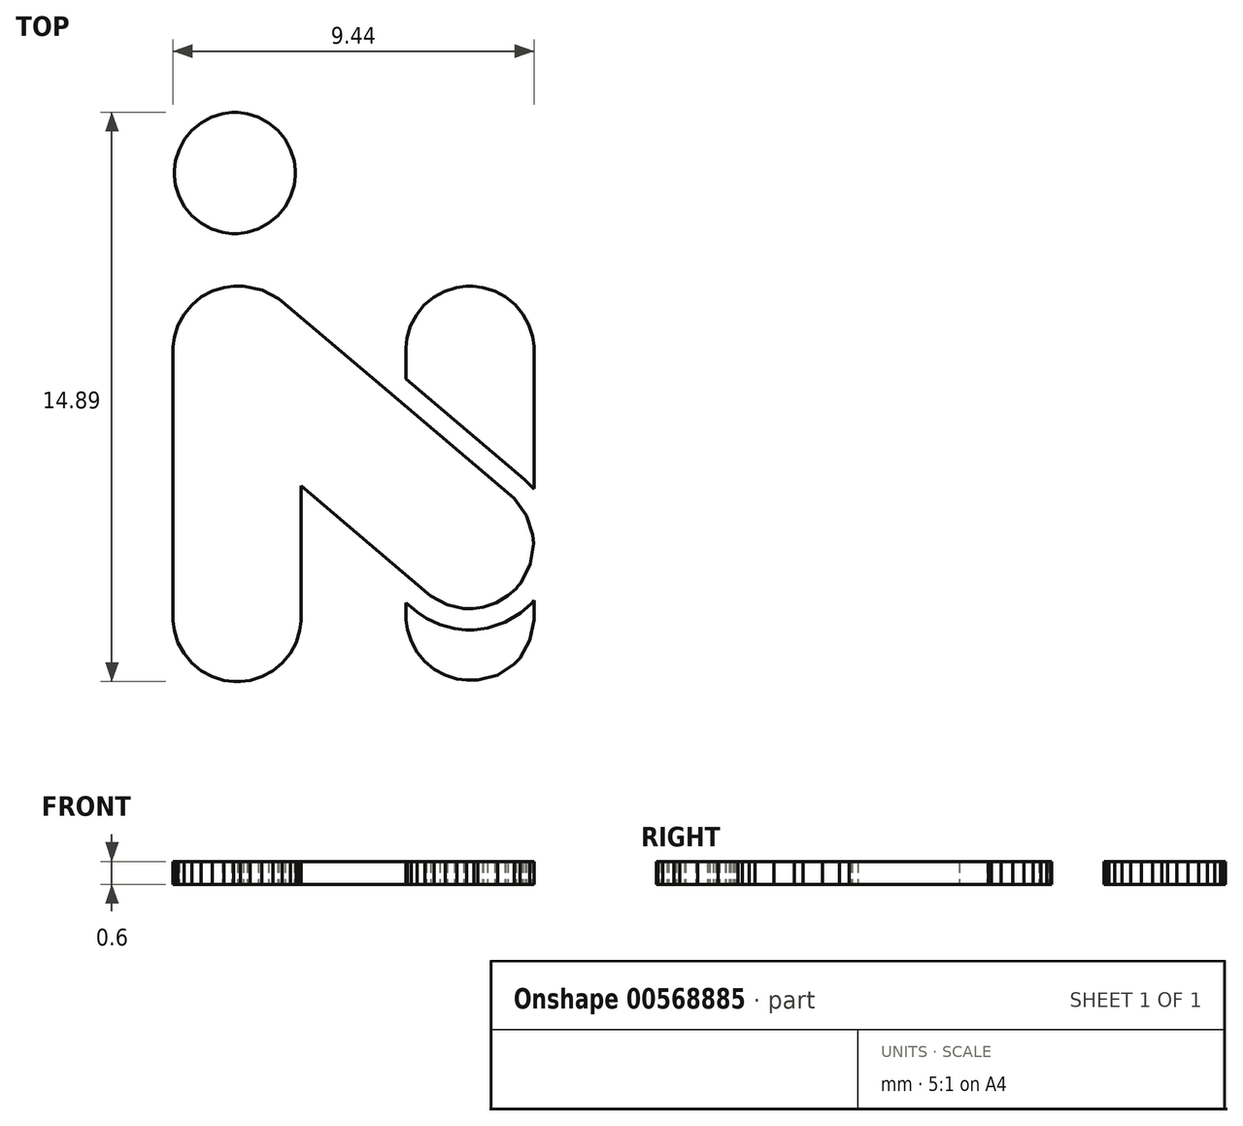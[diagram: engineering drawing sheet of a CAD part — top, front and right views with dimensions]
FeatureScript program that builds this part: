
annotation { "Feature Type Name" : "Feature", "Feature Type Description" : "" }
export const myFeature = defineFeature(function(context is Context, id is Id, definition is map)
    precondition{}
    {
        {
            var Q0;
            Q0=qCreatedBy(makeId("Top.planeOp"),FACE);
            var sketch = newSketch(context, id + "F0", { "sketchPlane" : qUnion([Q0])});
            skLineSegment(sketch, "E0", {"start": v(1.16, -1.13) * mm, "end": v(1.14, -1.15) * mm});
            skLineSegment(sketch, "E1", {"start": v(1.14, -1.15) * mm, "end": v(1.03, -1.22) * mm});
            skLineSegment(sketch, "E2", {"start": v(1.03, -1.22) * mm, "end": v(0.9, -1.25) * mm});
            skLineSegment(sketch, "E3", {"start": v(0.9, -1.25) * mm, "end": v(0.88, -1.26) * mm});
            skLineSegment(sketch, "E4", {"start": v(0.88, -1.26) * mm, "end": v(0.88, -1.26) * mm});
            skLineSegment(sketch, "E5", {"start": v(0.88, -1.26) * mm, "end": v(0.87, -1.26) * mm});
            skLineSegment(sketch, "E6", {"start": v(0.87, -1.26) * mm, "end": v(0.86, -1.26) * mm});
            skLineSegment(sketch, "E7", {"start": v(0.86, -1.26) * mm, "end": v(0.85, -1.26) * mm});
            skLineSegment(sketch, "E8", {"start": v(0.85, -1.26) * mm, "end": v(0.83, -1.26) * mm});
            skLineSegment(sketch, "E9", {"start": v(0.83, -1.26) * mm, "end": v(0.77, -1.25) * mm});
            skLineSegment(sketch, "E10", {"start": v(0.77, -1.25) * mm, "end": v(0.7, -1.22) * mm});
            skLineSegment(sketch, "E11", {"start": v(0.7, -1.22) * mm, "end": v(0.62, -1.18) * mm});
            skLineSegment(sketch, "E12", {"start": v(0.62, -1.18) * mm, "end": v(0.56, -1.13) * mm});
            skLineSegment(sketch, "E13", {"start": v(0.56, -1.13) * mm, "end": v(0.5, -1.07) * mm});
            skLineSegment(sketch, "E14", {"start": v(0.5, -1.07) * mm, "end": v(0.47, -1) * mm});
            skLineSegment(sketch, "E15", {"start": v(0.47, -1) * mm, "end": v(0.44, -0.92) * mm});
            skLineSegment(sketch, "E16", {"start": v(0.44, -0.92) * mm, "end": v(0.43, -0.86) * mm});
            skLineSegment(sketch, "E17", {"start": v(0.43, -0.86) * mm, "end": v(0.43, -0.84) * mm});
            skLineSegment(sketch, "E18", {"start": v(0.43, -0.84) * mm, "end": v(0.43, -0.75) * mm});
            skLineSegment(sketch, "E19", {"start": v(0.43, -0.75) * mm, "end": v(0.49, -0.8) * mm});
            skLineSegment(sketch, "E20", {"start": v(0.49, -0.8) * mm, "end": v(0.5, -0.8) * mm});
            skLineSegment(sketch, "E21", {"start": v(0.5, -0.8) * mm, "end": v(0.57, -0.85) * mm});
            skLineSegment(sketch, "E22", {"start": v(0.57, -0.85) * mm, "end": v(0.66, -0.9) * mm});
            skLineSegment(sketch, "E23", {"start": v(0.66, -0.9) * mm, "end": v(0.75, -0.92) * mm});
            skLineSegment(sketch, "E24", {"start": v(0.75, -0.92) * mm, "end": v(0.83, -0.93) * mm});
            skLineSegment(sketch, "E25", {"start": v(0.83, -0.93) * mm, "end": v(0.85, -0.93) * mm});
            skLineSegment(sketch, "E26", {"start": v(0.85, -0.93) * mm, "end": v(0.88, -0.93) * mm});
            skLineSegment(sketch, "E27", {"start": v(0.88, -0.93) * mm, "end": v(0.97, -0.91) * mm});
            skLineSegment(sketch, "E28", {"start": v(0.97, -0.91) * mm, "end": v(1.08, -0.88) * mm});
            skLineSegment(sketch, "E29", {"start": v(1.08, -0.88) * mm, "end": v(1.19, -0.81) * mm});
            skLineSegment(sketch, "E30", {"start": v(1.19, -0.81) * mm, "end": v(1.25, -0.75) * mm});
            skLineSegment(sketch, "E31", {"start": v(1.25, -0.75) * mm, "end": v(1.27, -0.73) * mm});
            skLineSegment(sketch, "E32", {"start": v(1.27, -0.73) * mm, "end": v(1.27, -0.83) * mm});
            skLineSegment(sketch, "E33", {"start": v(1.27, -0.83) * mm, "end": v(1.27, -0.86) * mm});
            skLineSegment(sketch, "E34", {"start": v(1.27, -0.86) * mm, "end": v(1.25, -1) * mm});
            skLineSegment(sketch, "E35", {"start": v(1.25, -1) * mm, "end": v(1.18, -1.11) * mm});
            skLineSegment(sketch, "E36", {"start": v(1.18, -1.11) * mm, "end": v(1.16, -1.13) * mm});
            skLineSegment(sketch, "E37", {"start": v(-0.25, 0.02) * mm, "end": v(-0.25, -0.85) * mm});
            skLineSegment(sketch, "E38", {"start": v(-0.25, -0.85) * mm, "end": v(-0.25, -0.87) * mm});
            skLineSegment(sketch, "E39", {"start": v(-0.25, -0.87) * mm, "end": v(-0.26, -0.93) * mm});
            skLineSegment(sketch, "E40", {"start": v(-0.26, -0.93) * mm, "end": v(-0.28, -1) * mm});
            skLineSegment(sketch, "E41", {"start": v(-0.28, -1) * mm, "end": v(-0.32, -1.08) * mm});
            skLineSegment(sketch, "E42", {"start": v(-0.32, -1.08) * mm, "end": v(-0.37, -1.14) * mm});
            skLineSegment(sketch, "E43", {"start": v(-0.37, -1.14) * mm, "end": v(-0.44, -1.2) * mm});
            skLineSegment(sketch, "E44", {"start": v(-0.44, -1.2) * mm, "end": v(-0.5, -1.23) * mm});
            skLineSegment(sketch, "E45", {"start": v(-0.5, -1.23) * mm, "end": v(-0.59, -1.26) * mm});
            skLineSegment(sketch, "E46", {"start": v(-0.59, -1.26) * mm, "end": v(-0.65, -1.26) * mm});
            skLineSegment(sketch, "E47", {"start": v(-0.65, -1.26) * mm, "end": v(-0.67, -1.26) * mm});
            skLineSegment(sketch, "E48", {"start": v(-0.67, -1.26) * mm, "end": v(-0.7, -1.26) * mm});
            skLineSegment(sketch, "E49", {"start": v(-0.7, -1.26) * mm, "end": v(-0.75, -1.26) * mm});
            skLineSegment(sketch, "E50", {"start": v(-0.75, -1.26) * mm, "end": v(-0.83, -1.23) * mm});
            skLineSegment(sketch, "E51", {"start": v(-0.83, -1.23) * mm, "end": v(-0.9, -1.2) * mm});
            skLineSegment(sketch, "E52", {"start": v(-0.9, -1.2) * mm, "end": v(-0.97, -1.14) * mm});
            skLineSegment(sketch, "E53", {"start": v(-0.97, -1.14) * mm, "end": v(-1.02, -1.08) * mm});
            skLineSegment(sketch, "E54", {"start": v(-1.02, -1.08) * mm, "end": v(-1.06, -1) * mm});
            skLineSegment(sketch, "E55", {"start": v(-1.06, -1) * mm, "end": v(-1.08, -0.93) * mm});
            skLineSegment(sketch, "E56", {"start": v(-1.08, -0.93) * mm, "end": v(-1.09, -0.87) * mm});
            skLineSegment(sketch, "E57", {"start": v(-1.09, -0.87) * mm, "end": v(-1.09, -0.85) * mm});
            skLineSegment(sketch, "E58", {"start": v(-1.09, -0.85) * mm, "end": v(-1.09, 0.9) * mm});
            skLineSegment(sketch, "E59", {"start": v(-1.09, 0.9) * mm, "end": v(-1.09, 0.92) * mm});
            skLineSegment(sketch, "E60", {"start": v(-1.09, 0.92) * mm, "end": v(-1.08, 0.99) * mm});
            skLineSegment(sketch, "E61", {"start": v(-1.08, 0.99) * mm, "end": v(-1.06, 1.07) * mm});
            skLineSegment(sketch, "E62", {"start": v(-1.06, 1.07) * mm, "end": v(-1.02, 1.14) * mm});
            skLineSegment(sketch, "E63", {"start": v(-1.02, 1.14) * mm, "end": v(-0.97, 1.2) * mm});
            skLineSegment(sketch, "E64", {"start": v(-0.97, 1.2) * mm, "end": v(-0.9, 1.25) * mm});
            skLineSegment(sketch, "E65", {"start": v(-0.9, 1.25) * mm, "end": v(-0.83, 1.29) * mm});
            skLineSegment(sketch, "E66", {"start": v(-0.83, 1.29) * mm, "end": v(-0.75, 1.31) * mm});
            skLineSegment(sketch, "E67", {"start": v(-0.75, 1.31) * mm, "end": v(-0.7, 1.32) * mm});
            skLineSegment(sketch, "E68", {"start": v(-0.7, 1.32) * mm, "end": v(-0.67, 1.32) * mm});
            skLineSegment(sketch, "E69", {"start": v(-0.67, 1.32) * mm, "end": v(-0.67, 1.32) * mm});
            skLineSegment(sketch, "E70", {"start": v(-0.67, 1.32) * mm, "end": v(-0.66, 1.32) * mm});
            skLineSegment(sketch, "E71", {"start": v(-0.66, 1.32) * mm, "end": v(-0.66, 1.32) * mm});
            skLineSegment(sketch, "E72", {"start": v(-0.66, 1.32) * mm, "end": v(-0.65, 1.32) * mm});
            skLineSegment(sketch, "E73", {"start": v(-0.65, 1.32) * mm, "end": v(-0.65, 1.32) * mm});
            skLineSegment(sketch, "E74", {"start": v(-0.65, 1.32) * mm, "end": v(-0.63, 1.32) * mm});
            skLineSegment(sketch, "E75", {"start": v(-0.63, 1.32) * mm, "end": v(-0.5, 1.3) * mm});
            skLineSegment(sketch, "E76", {"start": v(-0.5, 1.3) * mm, "end": v(-0.4, 1.24) * mm});
            skLineSegment(sketch, "E77", {"start": v(-0.4, 1.24) * mm, "end": v(-0.38, 1.22) * mm});
            skLineSegment(sketch, "E78", {"start": v(-0.38, 1.22) * mm, "end": v(0.32, 0.63) * mm});
            skLineSegment(sketch, "E79", {"start": v(0.32, 0.63) * mm, "end": v(0.36, 0.68) * mm});
            skLineSegment(sketch, "E80", {"start": v(0.36, 0.68) * mm, "end": v(0.32, 0.63) * mm});
            skLineSegment(sketch, "E81", {"start": v(0.32, 0.63) * mm, "end": v(1.12, -0.05) * mm});
            skLineSegment(sketch, "E82", {"start": v(1.12, -0.05) * mm, "end": v(1.14, -0.07) * mm});
            skLineSegment(sketch, "E83", {"start": v(1.14, -0.07) * mm, "end": v(1.22, -0.18) * mm});
            skLineSegment(sketch, "E84", {"start": v(1.22, -0.18) * mm, "end": v(1.27, -0.3) * mm});
            skLineSegment(sketch, "E85", {"start": v(1.27, -0.3) * mm, "end": v(1.27, -0.33) * mm});
            skLineSegment(sketch, "E86", {"start": v(1.27, -0.33) * mm, "end": v(1.27, -0.36) * mm});
            skLineSegment(sketch, "E87", {"start": v(1.27, -0.36) * mm, "end": v(1.25, -0.5) * mm});
            skLineSegment(sketch, "E88", {"start": v(1.25, -0.5) * mm, "end": v(1.19, -0.62) * mm});
            skLineSegment(sketch, "E89", {"start": v(1.19, -0.62) * mm, "end": v(1.17, -0.64) * mm});
            skLineSegment(sketch, "E90", {"start": v(1.17, -0.64) * mm, "end": v(1.15, -0.66) * mm});
            skLineSegment(sketch, "E91", {"start": v(1.15, -0.66) * mm, "end": v(1.1, -0.7) * mm});
            skLineSegment(sketch, "E92", {"start": v(1.1, -0.7) * mm, "end": v(1.03, -0.75) * mm});
            skLineSegment(sketch, "E93", {"start": v(1.03, -0.75) * mm, "end": v(0.94, -0.78) * mm});
            skLineSegment(sketch, "E94", {"start": v(0.94, -0.78) * mm, "end": v(0.87, -0.79) * mm});
            skLineSegment(sketch, "E95", {"start": v(0.87, -0.79) * mm, "end": v(0.85, -0.79) * mm});
            skLineSegment(sketch, "E96", {"start": v(0.85, -0.79) * mm, "end": v(0.81, -0.79) * mm});
            skLineSegment(sketch, "E97", {"start": v(0.81, -0.79) * mm, "end": v(0.7, -0.76) * mm});
            skLineSegment(sketch, "E98", {"start": v(0.7, -0.76) * mm, "end": v(0.6, -0.7) * mm});
            skLineSegment(sketch, "E99", {"start": v(0.6, -0.7) * mm, "end": v(0.58, -0.69) * mm});
            skLineSegment(sketch, "E100", {"start": v(0.58, -0.69) * mm, "end": v(0.41, -0.54) * mm});
            skLineSegment(sketch, "E101", {"start": v(0.41, -0.54) * mm, "end": v(-0.25, 0.02) * mm});
            skLineSegment(sketch, "E102", {"start": v(0.85, 1.32) * mm, "end": v(0.85, 1.32) * mm});
            skLineSegment(sketch, "E103", {"start": v(0.85, 1.32) * mm, "end": v(0.87, 1.32) * mm});
            skLineSegment(sketch, "E104", {"start": v(0.87, 1.32) * mm, "end": v(0.94, 1.31) * mm});
            skLineSegment(sketch, "E105", {"start": v(0.94, 1.31) * mm, "end": v(1.02, 1.29) * mm});
            skLineSegment(sketch, "E106", {"start": v(1.02, 1.29) * mm, "end": v(1.09, 1.25) * mm});
            skLineSegment(sketch, "E107", {"start": v(1.09, 1.25) * mm, "end": v(1.15, 1.2) * mm});
            skLineSegment(sketch, "E108", {"start": v(1.15, 1.2) * mm, "end": v(1.2, 1.14) * mm});
            skLineSegment(sketch, "E109", {"start": v(1.2, 1.14) * mm, "end": v(1.24, 1.07) * mm});
            skLineSegment(sketch, "E110", {"start": v(1.24, 1.07) * mm, "end": v(1.26, 1) * mm});
            skLineSegment(sketch, "E111", {"start": v(1.26, 1) * mm, "end": v(1.27, 0.93) * mm});
            skLineSegment(sketch, "E112", {"start": v(1.27, 0.93) * mm, "end": v(1.27, 0.9) * mm});
            skLineSegment(sketch, "E113", {"start": v(1.27, 0.9) * mm, "end": v(1.27, 0) * mm});
            skLineSegment(sketch, "E114", {"start": v(1.27, 0) * mm, "end": v(1.27, 0) * mm});
            skLineSegment(sketch, "E115", {"start": v(1.27, 0) * mm, "end": v(1.22, 0.05) * mm});
            skLineSegment(sketch, "E116", {"start": v(1.22, 0.05) * mm, "end": v(1.21, 0.06) * mm});
            skLineSegment(sketch, "E117", {"start": v(1.21, 0.06) * mm, "end": v(0.43, 0.72) * mm});
            skLineSegment(sketch, "E118", {"start": v(0.43, 0.72) * mm, "end": v(0.43, 0.9) * mm});
            skLineSegment(sketch, "E119", {"start": v(0.43, 0.9) * mm, "end": v(0.43, 0.92) * mm});
            skLineSegment(sketch, "E120", {"start": v(0.43, 0.92) * mm, "end": v(0.44, 0.98) * mm});
            skLineSegment(sketch, "E121", {"start": v(0.44, 0.98) * mm, "end": v(0.47, 1.06) * mm});
            skLineSegment(sketch, "E122", {"start": v(0.47, 1.06) * mm, "end": v(0.5, 1.13) * mm});
            skLineSegment(sketch, "E123", {"start": v(0.5, 1.13) * mm, "end": v(0.55, 1.2) * mm});
            skLineSegment(sketch, "E124", {"start": v(0.55, 1.2) * mm, "end": v(0.62, 1.25) * mm});
            skLineSegment(sketch, "E125", {"start": v(0.62, 1.25) * mm, "end": v(0.69, 1.29) * mm});
            skLineSegment(sketch, "E126", {"start": v(0.69, 1.29) * mm, "end": v(0.77, 1.31) * mm});
            skLineSegment(sketch, "E127", {"start": v(0.77, 1.31) * mm, "end": v(0.83, 1.32) * mm});
            skLineSegment(sketch, "E128", {"start": v(0.83, 1.32) * mm, "end": v(0.85, 1.32) * mm});
            skLineSegment(sketch, "E129", {"start": v(1.41, 0.9) * mm, "end": v(1.41, 0.94) * mm});
            skLineSegment(sketch, "E130", {"start": v(1.41, 0.94) * mm, "end": v(1.4, 1.02) * mm});
            skLineSegment(sketch, "E131", {"start": v(1.4, 1.02) * mm, "end": v(1.37, 1.12) * mm});
            skLineSegment(sketch, "E132", {"start": v(1.37, 1.12) * mm, "end": v(1.31, 1.22) * mm});
            skLineSegment(sketch, "E133", {"start": v(1.31, 1.22) * mm, "end": v(1.25, 1.3) * mm});
            skLineSegment(sketch, "E134", {"start": v(1.25, 1.3) * mm, "end": v(1.16, 1.37) * mm});
            skLineSegment(sketch, "E135", {"start": v(1.16, 1.37) * mm, "end": v(1.07, 1.42) * mm});
            skLineSegment(sketch, "E136", {"start": v(1.07, 1.42) * mm, "end": v(0.96, 1.45) * mm});
            skLineSegment(sketch, "E137", {"start": v(0.96, 1.45) * mm, "end": v(0.88, 1.46) * mm});
            skLineSegment(sketch, "E138", {"start": v(0.88, 1.46) * mm, "end": v(0.85, 1.46) * mm});
            skLineSegment(sketch, "E139", {"start": v(0.85, 1.46) * mm, "end": v(0.85, 1.46) * mm});
            skLineSegment(sketch, "E140", {"start": v(0.85, 1.46) * mm, "end": v(0.82, 1.46) * mm});
            skLineSegment(sketch, "E141", {"start": v(0.82, 1.46) * mm, "end": v(0.74, 1.45) * mm});
            skLineSegment(sketch, "E142", {"start": v(0.74, 1.45) * mm, "end": v(0.63, 1.41) * mm});
            skLineSegment(sketch, "E143", {"start": v(0.63, 1.41) * mm, "end": v(0.54, 1.36) * mm});
            skLineSegment(sketch, "E144", {"start": v(0.54, 1.36) * mm, "end": v(0.46, 1.3) * mm});
            skLineSegment(sketch, "E145", {"start": v(0.46, 1.3) * mm, "end": v(0.39, 1.2) * mm});
            skLineSegment(sketch, "E146", {"start": v(0.39, 1.2) * mm, "end": v(0.34, 1.11) * mm});
            skLineSegment(sketch, "E147", {"start": v(0.34, 1.11) * mm, "end": v(0.3, 1) * mm});
            skLineSegment(sketch, "E148", {"start": v(0.3, 1) * mm, "end": v(0.3, 0.93) * mm});
            skLineSegment(sketch, "E149", {"start": v(0.3, 0.93) * mm, "end": v(0.3, 0.9) * mm});
            skLineSegment(sketch, "E150", {"start": v(0.3, 0.9) * mm, "end": v(0.3, 0.83) * mm});
            skLineSegment(sketch, "E151", {"start": v(0.3, 0.83) * mm, "end": v(-0.29, 1.33) * mm});
            skLineSegment(sketch, "E152", {"start": v(-0.29, 1.33) * mm, "end": v(-0.3, 1.34) * mm});
            skLineSegment(sketch, "E153", {"start": v(-0.3, 1.34) * mm, "end": v(-0.37, 1.38) * mm});
            skLineSegment(sketch, "E154", {"start": v(-0.37, 1.38) * mm, "end": v(-0.46, 1.43) * mm});
            skLineSegment(sketch, "E155", {"start": v(-0.46, 1.43) * mm, "end": v(-0.55, 1.45) * mm});
            skLineSegment(sketch, "E156", {"start": v(-0.55, 1.45) * mm, "end": v(-0.62, 1.46) * mm});
            skLineSegment(sketch, "E157", {"start": v(-0.62, 1.46) * mm, "end": v(-0.65, 1.46) * mm});
            skLineSegment(sketch, "E158", {"start": v(-0.65, 1.46) * mm, "end": v(-0.65, 1.46) * mm});
            skLineSegment(sketch, "E159", {"start": v(-0.65, 1.46) * mm, "end": v(-0.67, 1.46) * mm});
            skLineSegment(sketch, "E160", {"start": v(-0.67, 1.46) * mm, "end": v(-0.67, 1.46) * mm});
            skLineSegment(sketch, "E161", {"start": v(-0.67, 1.46) * mm, "end": v(-0.7, 1.46) * mm});
            skLineSegment(sketch, "E162", {"start": v(-0.7, 1.46) * mm, "end": v(-0.78, 1.45) * mm});
            skLineSegment(sketch, "E163", {"start": v(-0.78, 1.45) * mm, "end": v(-0.89, 1.42) * mm});
            skLineSegment(sketch, "E164", {"start": v(-0.89, 1.42) * mm, "end": v(-0.98, 1.36) * mm});
            skLineSegment(sketch, "E165", {"start": v(-0.98, 1.36) * mm, "end": v(-1.06, 1.3) * mm});
            skLineSegment(sketch, "E166", {"start": v(-1.06, 1.3) * mm, "end": v(-1.13, 1.21) * mm});
            skLineSegment(sketch, "E167", {"start": v(-1.13, 1.21) * mm, "end": v(-1.18, 1.12) * mm});
            skLineSegment(sketch, "E168", {"start": v(-1.18, 1.12) * mm, "end": v(-1.22, 1.01) * mm});
            skLineSegment(sketch, "E169", {"start": v(-1.22, 1.01) * mm, "end": v(-1.23, 0.93) * mm});
            skLineSegment(sketch, "E170", {"start": v(-1.23, 0.93) * mm, "end": v(-1.23, 0.9) * mm});
            skLineSegment(sketch, "E171", {"start": v(-1.23, 0.9) * mm, "end": v(-1.23, -0.85) * mm});
            skLineSegment(sketch, "E172", {"start": v(-1.23, -0.85) * mm, "end": v(-1.23, -0.87) * mm});
            skLineSegment(sketch, "E173", {"start": v(-1.23, -0.87) * mm, "end": v(-1.22, -0.96) * mm});
            skLineSegment(sketch, "E174", {"start": v(-1.22, -0.96) * mm, "end": v(-1.18, -1.06) * mm});
            skLineSegment(sketch, "E175", {"start": v(-1.18, -1.06) * mm, "end": v(-1.13, -1.16) * mm});
            skLineSegment(sketch, "E176", {"start": v(-1.13, -1.16) * mm, "end": v(-1.06, -1.24) * mm});
            skLineSegment(sketch, "E177", {"start": v(-1.06, -1.24) * mm, "end": v(-0.98, -1.3) * mm});
            skLineSegment(sketch, "E178", {"start": v(-0.98, -1.3) * mm, "end": v(-0.89, -1.36) * mm});
            skLineSegment(sketch, "E179", {"start": v(-0.89, -1.36) * mm, "end": v(-0.78, -1.4) * mm});
            skLineSegment(sketch, "E180", {"start": v(-0.78, -1.4) * mm, "end": v(-0.7, -1.4) * mm});
            skLineSegment(sketch, "E181", {"start": v(-0.7, -1.4) * mm, "end": v(-0.67, -1.4) * mm});
            skLineSegment(sketch, "E182", {"start": v(-0.67, -1.4) * mm, "end": v(-0.64, -1.4) * mm});
            skLineSegment(sketch, "E183", {"start": v(-0.64, -1.4) * mm, "end": v(-0.56, -1.4) * mm});
            skLineSegment(sketch, "E184", {"start": v(-0.56, -1.4) * mm, "end": v(-0.45, -1.36) * mm});
            skLineSegment(sketch, "E185", {"start": v(-0.45, -1.36) * mm, "end": v(-0.36, -1.3) * mm});
            skLineSegment(sketch, "E186", {"start": v(-0.36, -1.3) * mm, "end": v(-0.27, -1.24) * mm});
            skLineSegment(sketch, "E187", {"start": v(-0.27, -1.24) * mm, "end": v(-0.2, -1.16) * mm});
            skLineSegment(sketch, "E188", {"start": v(-0.2, -1.16) * mm, "end": v(-0.16, -1.06) * mm});
            skLineSegment(sketch, "E189", {"start": v(-0.16, -1.06) * mm, "end": v(-0.12, -0.96) * mm});
            skLineSegment(sketch, "E190", {"start": v(-0.12, -0.96) * mm, "end": v(-0.11, -0.87) * mm});
            skLineSegment(sketch, "E191", {"start": v(-0.11, -0.87) * mm, "end": v(-0.11, -0.85) * mm});
            skLineSegment(sketch, "E192", {"start": v(-0.11, -0.85) * mm, "end": v(-0.11, -0.28) * mm});
            skLineSegment(sketch, "E193", {"start": v(-0.11, -0.28) * mm, "end": v(0.3, -0.63) * mm});
            skLineSegment(sketch, "E194", {"start": v(0.3, -0.63) * mm, "end": v(0.3, -0.84) * mm});
            skLineSegment(sketch, "E195", {"start": v(0.3, -0.84) * mm, "end": v(0.3, -0.87) * mm});
            skLineSegment(sketch, "E196", {"start": v(0.3, -0.87) * mm, "end": v(0.3, -0.95) * mm});
            skLineSegment(sketch, "E197", {"start": v(0.3, -0.95) * mm, "end": v(0.34, -1.06) * mm});
            skLineSegment(sketch, "E198", {"start": v(0.34, -1.06) * mm, "end": v(0.4, -1.15) * mm});
            skLineSegment(sketch, "E199", {"start": v(0.4, -1.15) * mm, "end": v(0.46, -1.23) * mm});
            skLineSegment(sketch, "E200", {"start": v(0.46, -1.23) * mm, "end": v(0.54, -1.3) * mm});
            skLineSegment(sketch, "E201", {"start": v(0.54, -1.3) * mm, "end": v(0.64, -1.35) * mm});
            skLineSegment(sketch, "E202", {"start": v(0.64, -1.35) * mm, "end": v(0.74, -1.38) * mm});
            skLineSegment(sketch, "E203", {"start": v(0.74, -1.38) * mm, "end": v(0.83, -1.4) * mm});
            skLineSegment(sketch, "E204", {"start": v(0.83, -1.4) * mm, "end": v(0.85, -1.4) * mm});
            skLineSegment(sketch, "E205", {"start": v(0.85, -1.4) * mm, "end": v(0.86, -1.4) * mm});
            skLineSegment(sketch, "E206", {"start": v(0.86, -1.4) * mm, "end": v(0.87, -1.4) * mm});
            skLineSegment(sketch, "E207", {"start": v(0.87, -1.4) * mm, "end": v(0.88, -1.4) * mm});
            skLineSegment(sketch, "E208", {"start": v(0.88, -1.4) * mm, "end": v(0.88, -1.4) * mm});
            skLineSegment(sketch, "E209", {"start": v(0.88, -1.4) * mm, "end": v(0.9, -1.4) * mm});
            skLineSegment(sketch, "E210", {"start": v(0.9, -1.4) * mm, "end": v(0.99, -1.38) * mm});
            skLineSegment(sketch, "E211", {"start": v(0.99, -1.38) * mm, "end": v(1.1, -1.35) * mm});
            skLineSegment(sketch, "E212", {"start": v(1.1, -1.35) * mm, "end": v(1.18, -1.3) * mm});
            skLineSegment(sketch, "E213", {"start": v(1.18, -1.3) * mm, "end": v(1.25, -1.24) * mm});
            skLineSegment(sketch, "E214", {"start": v(1.25, -1.24) * mm, "end": v(1.26, -1.23) * mm});
            skLineSegment(sketch, "E215", {"start": v(1.26, -1.23) * mm, "end": v(1.28, -1.2) * mm});
            skLineSegment(sketch, "E216", {"start": v(1.28, -1.2) * mm, "end": v(1.33, -1.14) * mm});
            skLineSegment(sketch, "E217", {"start": v(1.33, -1.14) * mm, "end": v(1.37, -1.04) * mm});
            skLineSegment(sketch, "E218", {"start": v(1.37, -1.04) * mm, "end": v(1.4, -0.94) * mm});
            skLineSegment(sketch, "E219", {"start": v(1.4, -0.94) * mm, "end": v(1.41, -0.86) * mm});
            skLineSegment(sketch, "E220", {"start": v(1.41, -0.86) * mm, "end": v(1.41, -0.83) * mm});
            skLineSegment(sketch, "E221", {"start": v(1.41, -0.83) * mm, "end": v(1.41, 0.9) * mm});
            skLineSegment(sketch, "E222", {"start": v(-0.68, 2.46) * mm, "end": v(-0.66, 2.46) * mm});
            skLineSegment(sketch, "E223", {"start": v(-0.66, 2.46) * mm, "end": v(-0.6, 2.45) * mm});
            skLineSegment(sketch, "E224", {"start": v(-0.6, 2.45) * mm, "end": v(-0.53, 2.43) * mm});
            skLineSegment(sketch, "E225", {"start": v(-0.53, 2.43) * mm, "end": v(-0.46, 2.39) * mm});
            skLineSegment(sketch, "E226", {"start": v(-0.46, 2.39) * mm, "end": v(-0.4, 2.34) * mm});
            skLineSegment(sketch, "E227", {"start": v(-0.4, 2.34) * mm, "end": v(-0.36, 2.28) * mm});
            skLineSegment(sketch, "E228", {"start": v(-0.36, 2.28) * mm, "end": v(-0.32, 2.21) * mm});
            skLineSegment(sketch, "E229", {"start": v(-0.32, 2.21) * mm, "end": v(-0.3, 2.14) * mm});
            skLineSegment(sketch, "E230", {"start": v(-0.3, 2.14) * mm, "end": v(-0.29, 2.08) * mm});
            skLineSegment(sketch, "E231", {"start": v(-0.29, 2.08) * mm, "end": v(-0.29, 2.06) * mm});
            skLineSegment(sketch, "E232", {"start": v(-0.29, 2.06) * mm, "end": v(-0.29, 2.04) * mm});
            skLineSegment(sketch, "E233", {"start": v(-0.29, 2.04) * mm, "end": v(-0.3, 1.98) * mm});
            skLineSegment(sketch, "E234", {"start": v(-0.3, 1.98) * mm, "end": v(-0.32, 1.9) * mm});
            skLineSegment(sketch, "E235", {"start": v(-0.32, 1.9) * mm, "end": v(-0.36, 1.84) * mm});
            skLineSegment(sketch, "E236", {"start": v(-0.36, 1.84) * mm, "end": v(-0.4, 1.78) * mm});
            skLineSegment(sketch, "E237", {"start": v(-0.4, 1.78) * mm, "end": v(-0.46, 1.73) * mm});
            skLineSegment(sketch, "E238", {"start": v(-0.46, 1.73) * mm, "end": v(-0.53, 1.7) * mm});
            skLineSegment(sketch, "E239", {"start": v(-0.53, 1.7) * mm, "end": v(-0.6, 1.67) * mm});
            skLineSegment(sketch, "E240", {"start": v(-0.6, 1.67) * mm, "end": v(-0.66, 1.66) * mm});
            skLineSegment(sketch, "E241", {"start": v(-0.66, 1.66) * mm, "end": v(-0.68, 1.66) * mm});
            skLineSegment(sketch, "E242", {"start": v(-0.68, 1.66) * mm, "end": v(-0.7, 1.66) * mm});
            skLineSegment(sketch, "E243", {"start": v(-0.7, 1.66) * mm, "end": v(-0.76, 1.67) * mm});
            skLineSegment(sketch, "E244", {"start": v(-0.76, 1.67) * mm, "end": v(-0.84, 1.7) * mm});
            skLineSegment(sketch, "E245", {"start": v(-0.84, 1.7) * mm, "end": v(-0.9, 1.73) * mm});
            skLineSegment(sketch, "E246", {"start": v(-0.9, 1.73) * mm, "end": v(-0.96, 1.78) * mm});
            skLineSegment(sketch, "E247", {"start": v(-0.96, 1.78) * mm, "end": v(-1.01, 1.84) * mm});
            skLineSegment(sketch, "E248", {"start": v(-1.01, 1.84) * mm, "end": v(-1.05, 1.9) * mm});
            skLineSegment(sketch, "E249", {"start": v(-1.05, 1.9) * mm, "end": v(-1.07, 1.98) * mm});
            skLineSegment(sketch, "E250", {"start": v(-1.07, 1.98) * mm, "end": v(-1.08, 2.04) * mm});
            skLineSegment(sketch, "E251", {"start": v(-1.08, 2.04) * mm, "end": v(-1.08, 2.06) * mm});
            skLineSegment(sketch, "E252", {"start": v(-1.08, 2.06) * mm, "end": v(-1.08, 2.08) * mm});
            skLineSegment(sketch, "E253", {"start": v(-1.08, 2.08) * mm, "end": v(-1.07, 2.14) * mm});
            skLineSegment(sketch, "E254", {"start": v(-1.07, 2.14) * mm, "end": v(-1.05, 2.21) * mm});
            skLineSegment(sketch, "E255", {"start": v(-1.05, 2.21) * mm, "end": v(-1.01, 2.28) * mm});
            skLineSegment(sketch, "E256", {"start": v(-1.01, 2.28) * mm, "end": v(-0.96, 2.34) * mm});
            skLineSegment(sketch, "E257", {"start": v(-0.96, 2.34) * mm, "end": v(-0.9, 2.39) * mm});
            skLineSegment(sketch, "E258", {"start": v(-0.9, 2.39) * mm, "end": v(-0.84, 2.43) * mm});
            skLineSegment(sketch, "E259", {"start": v(-0.84, 2.43) * mm, "end": v(-0.76, 2.45) * mm});
            skLineSegment(sketch, "E260", {"start": v(-0.76, 2.45) * mm, "end": v(-0.7, 2.46) * mm});
            skLineSegment(sketch, "E261", {"start": v(-0.7, 2.46) * mm, "end": v(-0.68, 2.46) * mm});
            skLineSegment(sketch, "E262", {"start": v(-0.68, 1.53) * mm, "end": v(-0.66, 1.53) * mm});
            skLineSegment(sketch, "E263", {"start": v(-0.66, 1.53) * mm, "end": v(-0.58, 1.54) * mm});
            skLineSegment(sketch, "E264", {"start": v(-0.58, 1.54) * mm, "end": v(-0.48, 1.57) * mm});
            skLineSegment(sketch, "E265", {"start": v(-0.48, 1.57) * mm, "end": v(-0.38, 1.62) * mm});
            skLineSegment(sketch, "E266", {"start": v(-0.38, 1.62) * mm, "end": v(-0.3, 1.68) * mm});
            skLineSegment(sketch, "E267", {"start": v(-0.3, 1.68) * mm, "end": v(-0.24, 1.76) * mm});
            skLineSegment(sketch, "E268", {"start": v(-0.24, 1.76) * mm, "end": v(-0.2, 1.85) * mm});
            skLineSegment(sketch, "E269", {"start": v(-0.2, 1.85) * mm, "end": v(-0.16, 1.95) * mm});
            skLineSegment(sketch, "E270", {"start": v(-0.16, 1.95) * mm, "end": v(-0.15, 2.03) * mm});
            skLineSegment(sketch, "E271", {"start": v(-0.15, 2.03) * mm, "end": v(-0.15, 2.06) * mm});
            skLineSegment(sketch, "E272", {"start": v(-0.15, 2.06) * mm, "end": v(-0.15, 2.09) * mm});
            skLineSegment(sketch, "E273", {"start": v(-0.15, 2.09) * mm, "end": v(-0.16, 2.17) * mm});
            skLineSegment(sketch, "E274", {"start": v(-0.16, 2.17) * mm, "end": v(-0.2, 2.27) * mm});
            skLineSegment(sketch, "E275", {"start": v(-0.2, 2.27) * mm, "end": v(-0.24, 2.36) * mm});
            skLineSegment(sketch, "E276", {"start": v(-0.24, 2.36) * mm, "end": v(-0.3, 2.44) * mm});
            skLineSegment(sketch, "E277", {"start": v(-0.3, 2.44) * mm, "end": v(-0.38, 2.5) * mm});
            skLineSegment(sketch, "E278", {"start": v(-0.38, 2.5) * mm, "end": v(-0.48, 2.55) * mm});
            skLineSegment(sketch, "E279", {"start": v(-0.48, 2.55) * mm, "end": v(-0.58, 2.58) * mm});
            skLineSegment(sketch, "E280", {"start": v(-0.58, 2.58) * mm, "end": v(-0.66, 2.6) * mm});
            skLineSegment(sketch, "E281", {"start": v(-0.66, 2.6) * mm, "end": v(-0.68, 2.6) * mm});
            skLineSegment(sketch, "E282", {"start": v(-0.68, 2.6) * mm, "end": v(-0.71, 2.6) * mm});
            skLineSegment(sketch, "E283", {"start": v(-0.71, 2.6) * mm, "end": v(-0.8, 2.58) * mm});
            skLineSegment(sketch, "E284", {"start": v(-0.8, 2.58) * mm, "end": v(-0.9, 2.55) * mm});
            skLineSegment(sketch, "E285", {"start": v(-0.9, 2.55) * mm, "end": v(-0.98, 2.5) * mm});
            skLineSegment(sketch, "E286", {"start": v(-0.98, 2.5) * mm, "end": v(-1.06, 2.44) * mm});
            skLineSegment(sketch, "E287", {"start": v(-1.06, 2.44) * mm, "end": v(-1.13, 2.36) * mm});
            skLineSegment(sketch, "E288", {"start": v(-1.13, 2.36) * mm, "end": v(-1.18, 2.27) * mm});
            skLineSegment(sketch, "E289", {"start": v(-1.18, 2.27) * mm, "end": v(-1.2, 2.17) * mm});
            skLineSegment(sketch, "E290", {"start": v(-1.2, 2.17) * mm, "end": v(-1.22, 2.09) * mm});
            skLineSegment(sketch, "E291", {"start": v(-1.22, 2.09) * mm, "end": v(-1.22, 2.06) * mm});
            skLineSegment(sketch, "E292", {"start": v(-1.22, 2.06) * mm, "end": v(-1.22, 2.03) * mm});
            skLineSegment(sketch, "E293", {"start": v(-1.22, 2.03) * mm, "end": v(-1.2, 1.95) * mm});
            skLineSegment(sketch, "E294", {"start": v(-1.2, 1.95) * mm, "end": v(-1.18, 1.85) * mm});
            skLineSegment(sketch, "E295", {"start": v(-1.18, 1.85) * mm, "end": v(-1.13, 1.76) * mm});
            skLineSegment(sketch, "E296", {"start": v(-1.13, 1.76) * mm, "end": v(-1.06, 1.68) * mm});
            skLineSegment(sketch, "E297", {"start": v(-1.06, 1.68) * mm, "end": v(-0.98, 1.62) * mm});
            skLineSegment(sketch, "E298", {"start": v(-0.98, 1.62) * mm, "end": v(-0.9, 1.57) * mm});
            skLineSegment(sketch, "E299", {"start": v(-0.9, 1.57) * mm, "end": v(-0.8, 1.54) * mm});
            skLineSegment(sketch, "E300", {"start": v(-0.8, 1.54) * mm, "end": v(-0.71, 1.53) * mm});
            skLineSegment(sketch, "E301", {"start": v(-0.71, 1.53) * mm, "end": v(-0.68, 1.53) * mm});
            skLineSegment(sketch, "E302", {"start": v(-1.68, -1.93) * mm, "end": v(-1.68, -1.93) * mm});
            skLineSegment(sketch, "E303", {"start": v(-1.68, -1.93) * mm, "end": v(-1.65, -1.9) * mm});
            skLineSegment(sketch, "E304", {"start": v(-1.65, -1.9) * mm, "end": v(-1.65, -1.9) * mm});
            skLineSegment(sketch, "E305", {"start": v(-1.65, -1.9) * mm, "end": v(-1.62, -1.9) * mm});
            skLineSegment(sketch, "E306", {"start": v(-1.62, -1.9) * mm, "end": v(-1.6, -1.9) * mm});
            skLineSegment(sketch, "E307", {"start": v(-1.6, -1.9) * mm, "end": v(-1.6, -1.9) * mm});
            skLineSegment(sketch, "E308", {"start": v(-1.6, -1.9) * mm, "end": v(-1.57, -1.9) * mm});
            skLineSegment(sketch, "E309", {"start": v(-1.57, -1.9) * mm, "end": v(-1.56, -1.9) * mm});
            skLineSegment(sketch, "E310", {"start": v(-1.56, -1.9) * mm, "end": v(-1.56, -1.9) * mm});
            skLineSegment(sketch, "E311", {"start": v(-1.56, -1.9) * mm, "end": v(-1.54, -1.92) * mm});
            skLineSegment(sketch, "E312", {"start": v(-1.54, -1.92) * mm, "end": v(-1.54, -1.92) * mm});
            skLineSegment(sketch, "E313", {"start": v(-1.54, -1.92) * mm, "end": v(-1.53, -1.93) * mm});
            skLineSegment(sketch, "E314", {"start": v(-1.53, -1.93) * mm, "end": v(-1.53, -1.94) * mm});
            skLineSegment(sketch, "E315", {"start": v(-1.53, -1.94) * mm, "end": v(-1.53, -1.94) * mm});
            skLineSegment(sketch, "E316", {"start": v(-1.53, -1.94) * mm, "end": v(-1.52, -1.97) * mm});
            skLineSegment(sketch, "E317", {"start": v(-1.52, -1.97) * mm, "end": v(-1.52, -1.98) * mm});
            skLineSegment(sketch, "E318", {"start": v(-1.52, -1.98) * mm, "end": v(-1.52, -2.5) * mm});
            skLineSegment(sketch, "E319", {"start": v(-1.52, -2.5) * mm, "end": v(-1.52, -2.51) * mm});
            skLineSegment(sketch, "E320", {"start": v(-1.52, -2.51) * mm, "end": v(-1.52, -2.53) * mm});
            skLineSegment(sketch, "E321", {"start": v(-1.52, -2.53) * mm, "end": v(-1.52, -2.53) * mm});
            skLineSegment(sketch, "E322", {"start": v(-1.52, -2.53) * mm, "end": v(-1.52, -2.54) * mm});
            skLineSegment(sketch, "E323", {"start": v(-1.52, -2.54) * mm, "end": v(-1.53, -2.56) * mm});
            skLineSegment(sketch, "E324", {"start": v(-1.53, -2.56) * mm, "end": v(-1.53, -2.56) * mm});
            skLineSegment(sketch, "E325", {"start": v(-1.53, -2.56) * mm, "end": v(-1.56, -2.58) * mm});
            skLineSegment(sketch, "E326", {"start": v(-1.56, -2.58) * mm, "end": v(-1.6, -2.58) * mm});
            skLineSegment(sketch, "E327", {"start": v(-1.6, -2.58) * mm, "end": v(-1.6, -2.58) * mm});
            skLineSegment(sketch, "E328", {"start": v(-1.6, -2.58) * mm, "end": v(-1.61, -2.58) * mm});
            skLineSegment(sketch, "E329", {"start": v(-1.61, -2.58) * mm, "end": v(-1.64, -2.58) * mm});
            skLineSegment(sketch, "E330", {"start": v(-1.64, -2.58) * mm, "end": v(-1.65, -2.58) * mm});
            skLineSegment(sketch, "E331", {"start": v(-1.65, -2.58) * mm, "end": v(-1.66, -2.58) * mm});
            skLineSegment(sketch, "E332", {"start": v(-1.66, -2.58) * mm, "end": v(-1.66, -2.58) * mm});
            skLineSegment(sketch, "E333", {"start": v(-1.66, -2.58) * mm, "end": v(-1.68, -2.56) * mm});
            skLineSegment(sketch, "E334", {"start": v(-1.68, -2.56) * mm, "end": v(-1.68, -2.56) * mm});
            skLineSegment(sketch, "E335", {"start": v(-1.68, -2.56) * mm, "end": v(-1.7, -2.53) * mm});
            skLineSegment(sketch, "E336", {"start": v(-1.7, -2.53) * mm, "end": v(-1.77, -2.43) * mm});
            skLineSegment(sketch, "E337", {"start": v(-1.77, -2.43) * mm, "end": v(-1.85, -2.33) * mm});
            skLineSegment(sketch, "E338", {"start": v(-1.85, -2.33) * mm, "end": v(-1.91, -2.25) * mm});
            skLineSegment(sketch, "E339", {"start": v(-1.91, -2.25) * mm, "end": v(-1.94, -2.2) * mm});
            skLineSegment(sketch, "E340", {"start": v(-1.94, -2.2) * mm, "end": v(-1.96, -2.2) * mm});
            skLineSegment(sketch, "E341", {"start": v(-1.96, -2.2) * mm, "end": v(-1.96, -2.5) * mm});
            skLineSegment(sketch, "E342", {"start": v(-1.96, -2.5) * mm, "end": v(-1.96, -2.51) * mm});
            skLineSegment(sketch, "E343", {"start": v(-1.96, -2.51) * mm, "end": v(-1.96, -2.53) * mm});
            skLineSegment(sketch, "E344", {"start": v(-1.96, -2.53) * mm, "end": v(-1.96, -2.53) * mm});
            skLineSegment(sketch, "E345", {"start": v(-1.96, -2.53) * mm, "end": v(-1.96, -2.54) * mm});
            skLineSegment(sketch, "E346", {"start": v(-1.96, -2.54) * mm, "end": v(-1.96, -2.56) * mm});
            skLineSegment(sketch, "E347", {"start": v(-1.96, -2.56) * mm, "end": v(-1.97, -2.56) * mm});
            skLineSegment(sketch, "E348", {"start": v(-1.97, -2.56) * mm, "end": v(-1.97, -2.56) * mm});
            skLineSegment(sketch, "E349", {"start": v(-1.97, -2.56) * mm, "end": v(-2, -2.58) * mm});
            skLineSegment(sketch, "E350", {"start": v(-2, -2.58) * mm, "end": v(-2.03, -2.58) * mm});
            skLineSegment(sketch, "E351", {"start": v(-2.03, -2.58) * mm, "end": v(-2.04, -2.58) * mm});
            skLineSegment(sketch, "E352", {"start": v(-2.04, -2.58) * mm, "end": v(-2.05, -2.58) * mm});
            skLineSegment(sketch, "E353", {"start": v(-2.05, -2.58) * mm, "end": v(-2.08, -2.58) * mm});
            skLineSegment(sketch, "E354", {"start": v(-2.08, -2.58) * mm, "end": v(-2.1, -2.56) * mm});
            skLineSegment(sketch, "E355", {"start": v(-2.1, -2.56) * mm, "end": v(-2.1, -2.56) * mm});
            skLineSegment(sketch, "E356", {"start": v(-2.1, -2.56) * mm, "end": v(-2.11, -2.56) * mm});
            skLineSegment(sketch, "E357", {"start": v(-2.11, -2.56) * mm, "end": v(-2.12, -2.54) * mm});
            skLineSegment(sketch, "E358", {"start": v(-2.12, -2.54) * mm, "end": v(-2.12, -2.53) * mm});
            skLineSegment(sketch, "E359", {"start": v(-2.12, -2.53) * mm, "end": v(-2.12, -2.53) * mm});
            skLineSegment(sketch, "E360", {"start": v(-2.12, -2.53) * mm, "end": v(-2.12, -2.5) * mm});
            skLineSegment(sketch, "E361", {"start": v(-2.12, -2.5) * mm, "end": v(-2.12, -2.5) * mm});
            skLineSegment(sketch, "E362", {"start": v(-2.12, -2.5) * mm, "end": v(-2.12, -1.98) * mm});
            skLineSegment(sketch, "E363", {"start": v(-2.12, -1.98) * mm, "end": v(-2.12, -1.97) * mm});
            skLineSegment(sketch, "E364", {"start": v(-2.12, -1.97) * mm, "end": v(-2.12, -1.95) * mm});
            skLineSegment(sketch, "E365", {"start": v(-2.12, -1.95) * mm, "end": v(-2.11, -1.93) * mm});
            skLineSegment(sketch, "E366", {"start": v(-2.11, -1.93) * mm, "end": v(-2.11, -1.93) * mm});
            skLineSegment(sketch, "E367", {"start": v(-2.11, -1.93) * mm, "end": v(-2.1, -1.93) * mm});
            skLineSegment(sketch, "E368", {"start": v(-2.1, -1.93) * mm, "end": v(-2.09, -1.9) * mm});
            skLineSegment(sketch, "E369", {"start": v(-2.09, -1.9) * mm, "end": v(-2.08, -1.9) * mm});
            skLineSegment(sketch, "E370", {"start": v(-2.08, -1.9) * mm, "end": v(-2.08, -1.9) * mm});
            skLineSegment(sketch, "E371", {"start": v(-2.08, -1.9) * mm, "end": v(-2.05, -1.9) * mm});
            skLineSegment(sketch, "E372", {"start": v(-2.05, -1.9) * mm, "end": v(-2.04, -1.9) * mm});
            skLineSegment(sketch, "E373", {"start": v(-2.04, -1.9) * mm, "end": v(-2.03, -1.9) * mm});
            skLineSegment(sketch, "E374", {"start": v(-2.03, -1.9) * mm, "end": v(-2, -1.9) * mm});
            skLineSegment(sketch, "E375", {"start": v(-2, -1.9) * mm, "end": v(-2, -1.9) * mm});
            skLineSegment(sketch, "E376", {"start": v(-2, -1.9) * mm, "end": v(-1.97, -1.92) * mm});
            skLineSegment(sketch, "E377", {"start": v(-1.97, -1.92) * mm, "end": v(-1.97, -1.92) * mm});
            skLineSegment(sketch, "E378", {"start": v(-1.97, -1.92) * mm, "end": v(-1.96, -1.93) * mm});
            skLineSegment(sketch, "E379", {"start": v(-1.96, -1.93) * mm, "end": v(-1.95, -1.94) * mm});
            skLineSegment(sketch, "E380", {"start": v(-1.95, -1.94) * mm, "end": v(-1.95, -1.94) * mm});
            skLineSegment(sketch, "E381", {"start": v(-1.95, -1.94) * mm, "end": v(-1.93, -1.97) * mm});
            skLineSegment(sketch, "E382", {"start": v(-1.93, -1.97) * mm, "end": v(-1.86, -2.06) * mm});
            skLineSegment(sketch, "E383", {"start": v(-1.86, -2.06) * mm, "end": v(-1.79, -2.16) * mm});
            skLineSegment(sketch, "E384", {"start": v(-1.79, -2.16) * mm, "end": v(-1.73, -2.24) * mm});
            skLineSegment(sketch, "E385", {"start": v(-1.73, -2.24) * mm, "end": v(-1.7, -2.28) * mm});
            skLineSegment(sketch, "E386", {"start": v(-1.7, -2.28) * mm, "end": v(-1.69, -2.3) * mm});
            skLineSegment(sketch, "E387", {"start": v(-1.69, -2.3) * mm, "end": v(-1.69, -1.98) * mm});
            skLineSegment(sketch, "E388", {"start": v(-1.69, -1.98) * mm, "end": v(-1.69, -1.97) * mm});
            skLineSegment(sketch, "E389", {"start": v(-1.69, -1.97) * mm, "end": v(-1.68, -1.95) * mm});
            skLineSegment(sketch, "E390", {"start": v(-1.68, -1.95) * mm, "end": v(-1.68, -1.93) * mm});
            skLineSegment(sketch, "E391", {"start": v(-1.28, -2.42) * mm, "end": v(-1, -2.42) * mm});
            skLineSegment(sketch, "E392", {"start": v(-1, -2.42) * mm, "end": v(-0.99, -2.42) * mm});
            skLineSegment(sketch, "E393", {"start": v(-0.99, -2.42) * mm, "end": v(-0.96, -2.42) * mm});
            skLineSegment(sketch, "E394", {"start": v(-0.96, -2.42) * mm, "end": v(-0.96, -2.42) * mm});
            skLineSegment(sketch, "E395", {"start": v(-0.96, -2.42) * mm, "end": v(-0.94, -2.43) * mm});
            skLineSegment(sketch, "E396", {"start": v(-0.94, -2.43) * mm, "end": v(-0.94, -2.43) * mm});
            skLineSegment(sketch, "E397", {"start": v(-0.94, -2.43) * mm, "end": v(-0.93, -2.43) * mm});
            skLineSegment(sketch, "E398", {"start": v(-0.93, -2.43) * mm, "end": v(-0.92, -2.45) * mm});
            skLineSegment(sketch, "E399", {"start": v(-0.92, -2.45) * mm, "end": v(-0.91, -2.49) * mm});
            skLineSegment(sketch, "E400", {"start": v(-0.91, -2.49) * mm, "end": v(-0.91, -2.5) * mm});
            skLineSegment(sketch, "E401", {"start": v(-0.91, -2.5) * mm, "end": v(-0.91, -2.51) * mm});
            skLineSegment(sketch, "E402", {"start": v(-0.91, -2.51) * mm, "end": v(-0.92, -2.55) * mm});
            skLineSegment(sketch, "E403", {"start": v(-0.92, -2.55) * mm, "end": v(-0.94, -2.58) * mm});
            skLineSegment(sketch, "E404", {"start": v(-0.94, -2.58) * mm, "end": v(-0.95, -2.58) * mm});
            skLineSegment(sketch, "E405", {"start": v(-0.95, -2.58) * mm, "end": v(-0.95, -2.58) * mm});
            skLineSegment(sketch, "E406", {"start": v(-0.95, -2.58) * mm, "end": v(-0.98, -2.58) * mm});
            skLineSegment(sketch, "E407", {"start": v(-0.98, -2.58) * mm, "end": v(-1, -2.58) * mm});
            skLineSegment(sketch, "E408", {"start": v(-1, -2.58) * mm, "end": v(-1.37, -2.58) * mm});
            skLineSegment(sketch, "E409", {"start": v(-1.37, -2.58) * mm, "end": v(-1.38, -2.58) * mm});
            skLineSegment(sketch, "E410", {"start": v(-1.38, -2.58) * mm, "end": v(-1.42, -2.58) * mm});
            skLineSegment(sketch, "E411", {"start": v(-1.42, -2.58) * mm, "end": v(-1.44, -2.55) * mm});
            skLineSegment(sketch, "E412", {"start": v(-1.44, -2.55) * mm, "end": v(-1.44, -2.55) * mm});
            skLineSegment(sketch, "E413", {"start": v(-1.44, -2.55) * mm, "end": v(-1.45, -2.51) * mm});
            skLineSegment(sketch, "E414", {"start": v(-1.45, -2.51) * mm, "end": v(-1.45, -2.5) * mm});
            skLineSegment(sketch, "E415", {"start": v(-1.45, -2.5) * mm, "end": v(-1.45, -1.98) * mm});
            skLineSegment(sketch, "E416", {"start": v(-1.45, -1.98) * mm, "end": v(-1.45, -1.97) * mm});
            skLineSegment(sketch, "E417", {"start": v(-1.45, -1.97) * mm, "end": v(-1.44, -1.94) * mm});
            skLineSegment(sketch, "E418", {"start": v(-1.44, -1.94) * mm, "end": v(-1.43, -1.92) * mm});
            skLineSegment(sketch, "E419", {"start": v(-1.43, -1.92) * mm, "end": v(-1.43, -1.92) * mm});
            skLineSegment(sketch, "E420", {"start": v(-1.43, -1.92) * mm, "end": v(-1.43, -1.91) * mm});
            skLineSegment(sketch, "E421", {"start": v(-1.43, -1.91) * mm, "end": v(-1.4, -1.9) * mm});
            skLineSegment(sketch, "E422", {"start": v(-1.4, -1.9) * mm, "end": v(-1.37, -1.9) * mm});
            skLineSegment(sketch, "E423", {"start": v(-1.37, -1.9) * mm, "end": v(-1.36, -1.9) * mm});
            skLineSegment(sketch, "E424", {"start": v(-1.36, -1.9) * mm, "end": v(-1, -1.9) * mm});
            skLineSegment(sketch, "E425", {"start": v(-1, -1.9) * mm, "end": v(-0.99, -1.9) * mm});
            skLineSegment(sketch, "E426", {"start": v(-0.99, -1.9) * mm, "end": v(-0.96, -1.9) * mm});
            skLineSegment(sketch, "E427", {"start": v(-0.96, -1.9) * mm, "end": v(-0.96, -1.9) * mm});
            skLineSegment(sketch, "E428", {"start": v(-0.96, -1.9) * mm, "end": v(-0.94, -1.9) * mm});
            skLineSegment(sketch, "E429", {"start": v(-0.94, -1.9) * mm, "end": v(-0.94, -1.91) * mm});
            skLineSegment(sketch, "E430", {"start": v(-0.94, -1.91) * mm, "end": v(-0.93, -1.91) * mm});
            skLineSegment(sketch, "E431", {"start": v(-0.93, -1.91) * mm, "end": v(-0.92, -1.93) * mm});
            skLineSegment(sketch, "E432", {"start": v(-0.92, -1.93) * mm, "end": v(-0.91, -1.97) * mm});
            skLineSegment(sketch, "E433", {"start": v(-0.91, -1.97) * mm, "end": v(-0.91, -1.98) * mm});
            skLineSegment(sketch, "E434", {"start": v(-0.91, -1.98) * mm, "end": v(-0.91, -2) * mm});
            skLineSegment(sketch, "E435", {"start": v(-0.91, -2) * mm, "end": v(-0.92, -2.03) * mm});
            skLineSegment(sketch, "E436", {"start": v(-0.92, -2.03) * mm, "end": v(-0.94, -2.06) * mm});
            skLineSegment(sketch, "E437", {"start": v(-0.94, -2.06) * mm, "end": v(-0.95, -2.06) * mm});
            skLineSegment(sketch, "E438", {"start": v(-0.95, -2.06) * mm, "end": v(-0.95, -2.06) * mm});
            skLineSegment(sketch, "E439", {"start": v(-0.95, -2.06) * mm, "end": v(-0.98, -2.07) * mm});
            skLineSegment(sketch, "E440", {"start": v(-0.98, -2.07) * mm, "end": v(-1, -2.07) * mm});
            skLineSegment(sketch, "E441", {"start": v(-1, -2.07) * mm, "end": v(-1.28, -2.07) * mm});
            skLineSegment(sketch, "E442", {"start": v(-1.28, -2.07) * mm, "end": v(-1.28, -2.16) * mm});
            skLineSegment(sketch, "E443", {"start": v(-1.28, -2.16) * mm, "end": v(-1.1, -2.16) * mm});
            skLineSegment(sketch, "E444", {"start": v(-1.1, -2.16) * mm, "end": v(-1.09, -2.16) * mm});
            skLineSegment(sketch, "E445", {"start": v(-1.09, -2.16) * mm, "end": v(-1.07, -2.16) * mm});
            skLineSegment(sketch, "E446", {"start": v(-1.07, -2.16) * mm, "end": v(-1.07, -2.16) * mm});
            skLineSegment(sketch, "E447", {"start": v(-1.07, -2.16) * mm, "end": v(-1.06, -2.16) * mm});
            skLineSegment(sketch, "E448", {"start": v(-1.06, -2.16) * mm, "end": v(-1.04, -2.17) * mm});
            skLineSegment(sketch, "E449", {"start": v(-1.04, -2.17) * mm, "end": v(-1.04, -2.17) * mm});
            skLineSegment(sketch, "E450", {"start": v(-1.04, -2.17) * mm, "end": v(-1.02, -2.2) * mm});
            skLineSegment(sketch, "E451", {"start": v(-1.02, -2.2) * mm, "end": v(-1.02, -2.23) * mm});
            skLineSegment(sketch, "E452", {"start": v(-1.02, -2.23) * mm, "end": v(-1.02, -2.24) * mm});
            skLineSegment(sketch, "E453", {"start": v(-1.02, -2.24) * mm, "end": v(-1.02, -2.26) * mm});
            skLineSegment(sketch, "E454", {"start": v(-1.02, -2.26) * mm, "end": v(-1.02, -2.3) * mm});
            skLineSegment(sketch, "E455", {"start": v(-1.02, -2.3) * mm, "end": v(-1.04, -2.32) * mm});
            skLineSegment(sketch, "E456", {"start": v(-1.04, -2.32) * mm, "end": v(-1.05, -2.32) * mm});
            skLineSegment(sketch, "E457", {"start": v(-1.05, -2.32) * mm, "end": v(-1.05, -2.32) * mm});
            skLineSegment(sketch, "E458", {"start": v(-1.05, -2.32) * mm, "end": v(-1.09, -2.32) * mm});
            skLineSegment(sketch, "E459", {"start": v(-1.09, -2.32) * mm, "end": v(-1.1, -2.32) * mm});
            skLineSegment(sketch, "E460", {"start": v(-1.1, -2.32) * mm, "end": v(-1.28, -2.32) * mm});
            skLineSegment(sketch, "E461", {"start": v(-1.28, -2.32) * mm, "end": v(-1.28, -2.42) * mm});
            skLineSegment(sketch, "E462", {"start": v(-0.84, -2.49) * mm, "end": v(-0.85, -2.48) * mm});
            skLineSegment(sketch, "E463", {"start": v(-0.85, -2.48) * mm, "end": v(-0.86, -2.46) * mm});
            skLineSegment(sketch, "E464", {"start": v(-0.86, -2.46) * mm, "end": v(-0.87, -2.44) * mm});
            skLineSegment(sketch, "E465", {"start": v(-0.87, -2.44) * mm, "end": v(-0.87, -2.43) * mm});
            skLineSegment(sketch, "E466", {"start": v(-0.87, -2.43) * mm, "end": v(-0.87, -2.43) * mm});
            skLineSegment(sketch, "E467", {"start": v(-0.87, -2.43) * mm, "end": v(-0.86, -2.4) * mm});
            skLineSegment(sketch, "E468", {"start": v(-0.86, -2.4) * mm, "end": v(-0.83, -2.38) * mm});
            skLineSegment(sketch, "E469", {"start": v(-0.83, -2.38) * mm, "end": v(-0.83, -2.37) * mm});
            skLineSegment(sketch, "E470", {"start": v(-0.83, -2.37) * mm, "end": v(-0.82, -2.37) * mm});
            skLineSegment(sketch, "E471", {"start": v(-0.82, -2.37) * mm, "end": v(-0.79, -2.35) * mm});
            skLineSegment(sketch, "E472", {"start": v(-0.79, -2.35) * mm, "end": v(-0.78, -2.35) * mm});
            skLineSegment(sketch, "E473", {"start": v(-0.78, -2.35) * mm, "end": v(-0.77, -2.35) * mm});
            skLineSegment(sketch, "E474", {"start": v(-0.77, -2.35) * mm, "end": v(-0.74, -2.36) * mm});
            skLineSegment(sketch, "E475", {"start": v(-0.74, -2.36) * mm, "end": v(-0.71, -2.39) * mm});
            skLineSegment(sketch, "E476", {"start": v(-0.71, -2.39) * mm, "end": v(-0.7, -2.4) * mm});
            skLineSegment(sketch, "E477", {"start": v(-0.7, -2.4) * mm, "end": v(-0.7, -2.4) * mm});
            skLineSegment(sketch, "E478", {"start": v(-0.7, -2.4) * mm, "end": v(-0.67, -2.42) * mm});
            skLineSegment(sketch, "E479", {"start": v(-0.67, -2.42) * mm, "end": v(-0.67, -2.43) * mm});
            skLineSegment(sketch, "E480", {"start": v(-0.67, -2.43) * mm, "end": v(-0.66, -2.43) * mm});
            skLineSegment(sketch, "E481", {"start": v(-0.66, -2.43) * mm, "end": v(-0.63, -2.44) * mm});
            skLineSegment(sketch, "E482", {"start": v(-0.63, -2.44) * mm, "end": v(-0.62, -2.44) * mm});
            skLineSegment(sketch, "E483", {"start": v(-0.62, -2.44) * mm, "end": v(-0.61, -2.44) * mm});
            skLineSegment(sketch, "E484", {"start": v(-0.61, -2.44) * mm, "end": v(-0.58, -2.44) * mm});
            skLineSegment(sketch, "E485", {"start": v(-0.58, -2.44) * mm, "end": v(-0.56, -2.42) * mm});
            skLineSegment(sketch, "E486", {"start": v(-0.56, -2.42) * mm, "end": v(-0.54, -2.4) * mm});
            skLineSegment(sketch, "E487", {"start": v(-0.54, -2.4) * mm, "end": v(-0.53, -2.38) * mm});
            skLineSegment(sketch, "E488", {"start": v(-0.53, -2.38) * mm, "end": v(-0.53, -2.37) * mm});
            skLineSegment(sketch, "E489", {"start": v(-0.53, -2.37) * mm, "end": v(-0.53, -2.36) * mm});
            skLineSegment(sketch, "E490", {"start": v(-0.53, -2.36) * mm, "end": v(-0.54, -2.35) * mm});
            skLineSegment(sketch, "E491", {"start": v(-0.54, -2.35) * mm, "end": v(-0.55, -2.34) * mm});
            skLineSegment(sketch, "E492", {"start": v(-0.55, -2.34) * mm, "end": v(-0.56, -2.33) * mm});
            skLineSegment(sketch, "E493", {"start": v(-0.56, -2.33) * mm, "end": v(-0.56, -2.33) * mm});
            skLineSegment(sketch, "E494", {"start": v(-0.56, -2.33) * mm, "end": v(-0.61, -2.31) * mm});
            skLineSegment(sketch, "E495", {"start": v(-0.61, -2.31) * mm, "end": v(-0.62, -2.31) * mm});
            skLineSegment(sketch, "E496", {"start": v(-0.62, -2.31) * mm, "end": v(-0.62, -2.31) * mm});
            skLineSegment(sketch, "E497", {"start": v(-0.62, -2.31) * mm, "end": v(-0.69, -2.3) * mm});
            skLineSegment(sketch, "E498", {"start": v(-0.69, -2.3) * mm, "end": v(-0.7, -2.3) * mm});
            skLineSegment(sketch, "E499", {"start": v(-0.7, -2.3) * mm, "end": v(-0.7, -2.29) * mm});
            skLineSegment(sketch, "E500", {"start": v(-0.7, -2.29) * mm, "end": v(-0.76, -2.26) * mm});
            skLineSegment(sketch, "E501", {"start": v(-0.76, -2.26) * mm, "end": v(-0.77, -2.26) * mm});
            skLineSegment(sketch, "E502", {"start": v(-0.77, -2.26) * mm, "end": v(-0.78, -2.25) * mm});
            skLineSegment(sketch, "E503", {"start": v(-0.78, -2.25) * mm, "end": v(-0.8, -2.23) * mm});
            skLineSegment(sketch, "E504", {"start": v(-0.8, -2.23) * mm, "end": v(-0.83, -2.2) * mm});
            skLineSegment(sketch, "E505", {"start": v(-0.83, -2.2) * mm, "end": v(-0.83, -2.2) * mm});
            skLineSegment(sketch, "E506", {"start": v(-0.83, -2.2) * mm, "end": v(-0.83, -2.19) * mm});
            skLineSegment(sketch, "E507", {"start": v(-0.83, -2.19) * mm, "end": v(-0.85, -2.15) * mm});
            skLineSegment(sketch, "E508", {"start": v(-0.85, -2.15) * mm, "end": v(-0.85, -2.1) * mm});
            skLineSegment(sketch, "E509", {"start": v(-0.85, -2.1) * mm, "end": v(-0.85, -2.1) * mm});
            skLineSegment(sketch, "E510", {"start": v(-0.85, -2.1) * mm, "end": v(-0.85, -2.07) * mm});
            skLineSegment(sketch, "E511", {"start": v(-0.85, -2.07) * mm, "end": v(-0.84, -2.02) * mm});
            skLineSegment(sketch, "E512", {"start": v(-0.84, -2.02) * mm, "end": v(-0.8, -1.96) * mm});
            skLineSegment(sketch, "E513", {"start": v(-0.8, -1.96) * mm, "end": v(-0.8, -1.95) * mm});
            skLineSegment(sketch, "E514", {"start": v(-0.8, -1.95) * mm, "end": v(-0.78, -1.94) * mm});
            skLineSegment(sketch, "E515", {"start": v(-0.78, -1.94) * mm, "end": v(-0.72, -1.9) * mm});
            skLineSegment(sketch, "E516", {"start": v(-0.72, -1.9) * mm, "end": v(-0.65, -1.89) * mm});
            skLineSegment(sketch, "E517", {"start": v(-0.65, -1.89) * mm, "end": v(-0.63, -1.89) * mm});
            skLineSegment(sketch, "E518", {"start": v(-0.63, -1.89) * mm, "end": v(-0.6, -1.89) * mm});
            skLineSegment(sketch, "E519", {"start": v(-0.6, -1.89) * mm, "end": v(-0.53, -1.9) * mm});
            skLineSegment(sketch, "E520", {"start": v(-0.53, -1.9) * mm, "end": v(-0.52, -1.9) * mm});
            skLineSegment(sketch, "E521", {"start": v(-0.52, -1.9) * mm, "end": v(-0.52, -1.9) * mm});
            skLineSegment(sketch, "E522", {"start": v(-0.52, -1.9) * mm, "end": v(-0.48, -1.92) * mm});
            skLineSegment(sketch, "E523", {"start": v(-0.48, -1.92) * mm, "end": v(-0.46, -1.93) * mm});
            skLineSegment(sketch, "E524", {"start": v(-0.46, -1.93) * mm, "end": v(-0.46, -1.93) * mm});
            skLineSegment(sketch, "E525", {"start": v(-0.46, -1.93) * mm, "end": v(-0.44, -1.95) * mm});
            skLineSegment(sketch, "E526", {"start": v(-0.44, -1.95) * mm, "end": v(-0.43, -1.95) * mm});
            skLineSegment(sketch, "E527", {"start": v(-0.43, -1.95) * mm, "end": v(-0.41, -1.98) * mm});
            skLineSegment(sketch, "E528", {"start": v(-0.41, -1.98) * mm, "end": v(-0.4, -2) * mm});
            skLineSegment(sketch, "E529", {"start": v(-0.4, -2) * mm, "end": v(-0.4, -2) * mm});
            skLineSegment(sketch, "E530", {"start": v(-0.4, -2) * mm, "end": v(-0.41, -2.02) * mm});
            skLineSegment(sketch, "E531", {"start": v(-0.41, -2.02) * mm, "end": v(-0.43, -2.04) * mm});
            skLineSegment(sketch, "E532", {"start": v(-0.43, -2.04) * mm, "end": v(-0.43, -2.05) * mm});
            skLineSegment(sketch, "E533", {"start": v(-0.43, -2.05) * mm, "end": v(-0.44, -2.06) * mm});
            skLineSegment(sketch, "E534", {"start": v(-0.44, -2.06) * mm, "end": v(-0.46, -2.08) * mm});
            skLineSegment(sketch, "E535", {"start": v(-0.46, -2.08) * mm, "end": v(-0.49, -2.1) * mm});
            skLineSegment(sketch, "E536", {"start": v(-0.49, -2.1) * mm, "end": v(-0.5, -2.1) * mm});
            skLineSegment(sketch, "E537", {"start": v(-0.5, -2.1) * mm, "end": v(-0.5, -2.1) * mm});
            skLineSegment(sketch, "E538", {"start": v(-0.5, -2.1) * mm, "end": v(-0.52, -2.09) * mm});
            skLineSegment(sketch, "E539", {"start": v(-0.52, -2.09) * mm, "end": v(-0.54, -2.08) * mm});
            skLineSegment(sketch, "E540", {"start": v(-0.54, -2.08) * mm, "end": v(-0.54, -2.08) * mm});
            skLineSegment(sketch, "E541", {"start": v(-0.54, -2.08) * mm, "end": v(-0.54, -2.07) * mm});
            skLineSegment(sketch, "E542", {"start": v(-0.54, -2.07) * mm, "end": v(-0.55, -2.07) * mm});
            skLineSegment(sketch, "E543", {"start": v(-0.55, -2.07) * mm, "end": v(-0.55, -2.07) * mm});
            skLineSegment(sketch, "E544", {"start": v(-0.55, -2.07) * mm, "end": v(-0.56, -2.06) * mm});
            skLineSegment(sketch, "E545", {"start": v(-0.56, -2.06) * mm, "end": v(-0.57, -2.05) * mm});
            skLineSegment(sketch, "E546", {"start": v(-0.57, -2.05) * mm, "end": v(-0.57, -2.05) * mm});
            skLineSegment(sketch, "E547", {"start": v(-0.57, -2.05) * mm, "end": v(-0.6, -2.04) * mm});
            skLineSegment(sketch, "E548", {"start": v(-0.6, -2.04) * mm, "end": v(-0.62, -2.04) * mm});
            skLineSegment(sketch, "E549", {"start": v(-0.62, -2.04) * mm, "end": v(-0.63, -2.04) * mm});
            skLineSegment(sketch, "E550", {"start": v(-0.63, -2.04) * mm, "end": v(-0.67, -2.05) * mm});
            skLineSegment(sketch, "E551", {"start": v(-0.67, -2.05) * mm, "end": v(-0.67, -2.06) * mm});
            skLineSegment(sketch, "E552", {"start": v(-0.67, -2.06) * mm, "end": v(-0.67, -2.06) * mm});
            skLineSegment(sketch, "E553", {"start": v(-0.67, -2.06) * mm, "end": v(-0.68, -2.07) * mm});
            skLineSegment(sketch, "E554", {"start": v(-0.68, -2.07) * mm, "end": v(-0.69, -2.1) * mm});
            skLineSegment(sketch, "E555", {"start": v(-0.69, -2.1) * mm, "end": v(-0.69, -2.1) * mm});
            skLineSegment(sketch, "E556", {"start": v(-0.69, -2.1) * mm, "end": v(-0.68, -2.12) * mm});
            skLineSegment(sketch, "E557", {"start": v(-0.68, -2.12) * mm, "end": v(-0.67, -2.14) * mm});
            skLineSegment(sketch, "E558", {"start": v(-0.67, -2.14) * mm, "end": v(-0.67, -2.14) * mm});
            skLineSegment(sketch, "E559", {"start": v(-0.67, -2.14) * mm, "end": v(-0.66, -2.14) * mm});
            skLineSegment(sketch, "E560", {"start": v(-0.66, -2.14) * mm, "end": v(-0.61, -2.16) * mm});
            skLineSegment(sketch, "E561", {"start": v(-0.61, -2.16) * mm, "end": v(-0.6, -2.16) * mm});
            skLineSegment(sketch, "E562", {"start": v(-0.6, -2.16) * mm, "end": v(-0.6, -2.16) * mm});
            skLineSegment(sketch, "E563", {"start": v(-0.6, -2.16) * mm, "end": v(-0.54, -2.17) * mm});
            skLineSegment(sketch, "E564", {"start": v(-0.54, -2.17) * mm, "end": v(-0.53, -2.18) * mm});
            skLineSegment(sketch, "E565", {"start": v(-0.53, -2.18) * mm, "end": v(-0.52, -2.18) * mm});
            skLineSegment(sketch, "E566", {"start": v(-0.52, -2.18) * mm, "end": v(-0.46, -2.2) * mm});
            skLineSegment(sketch, "E567", {"start": v(-0.46, -2.2) * mm, "end": v(-0.45, -2.2) * mm});
            skLineSegment(sketch, "E568", {"start": v(-0.45, -2.2) * mm, "end": v(-0.45, -2.2) * mm});
            skLineSegment(sketch, "E569", {"start": v(-0.45, -2.2) * mm, "end": v(-0.42, -2.23) * mm});
            skLineSegment(sketch, "E570", {"start": v(-0.42, -2.23) * mm, "end": v(-0.4, -2.26) * mm});
            skLineSegment(sketch, "E571", {"start": v(-0.4, -2.26) * mm, "end": v(-0.4, -2.26) * mm});
            skLineSegment(sketch, "E572", {"start": v(-0.4, -2.26) * mm, "end": v(-0.39, -2.27) * mm});
            skLineSegment(sketch, "E573", {"start": v(-0.39, -2.27) * mm, "end": v(-0.37, -2.3) * mm});
            skLineSegment(sketch, "E574", {"start": v(-0.37, -2.3) * mm, "end": v(-0.37, -2.35) * mm});
            skLineSegment(sketch, "E575", {"start": v(-0.37, -2.35) * mm, "end": v(-0.37, -2.37) * mm});
            skLineSegment(sketch, "E576", {"start": v(-0.37, -2.37) * mm, "end": v(-0.37, -2.38) * mm});
            skLineSegment(sketch, "E577", {"start": v(-0.37, -2.38) * mm, "end": v(-0.37, -2.42) * mm});
            skLineSegment(sketch, "E578", {"start": v(-0.37, -2.42) * mm, "end": v(-0.39, -2.46) * mm});
            skLineSegment(sketch, "E579", {"start": v(-0.39, -2.46) * mm, "end": v(-0.4, -2.47) * mm});
            skLineSegment(sketch, "E580", {"start": v(-0.4, -2.47) * mm, "end": v(-0.4, -2.48) * mm});
            skLineSegment(sketch, "E581", {"start": v(-0.4, -2.48) * mm, "end": v(-0.42, -2.51) * mm});
            skLineSegment(sketch, "E582", {"start": v(-0.42, -2.51) * mm, "end": v(-0.45, -2.54) * mm});
            skLineSegment(sketch, "E583", {"start": v(-0.45, -2.54) * mm, "end": v(-0.46, -2.54) * mm});
            skLineSegment(sketch, "E584", {"start": v(-0.46, -2.54) * mm, "end": v(-0.47, -2.55) * mm});
            skLineSegment(sketch, "E585", {"start": v(-0.47, -2.55) * mm, "end": v(-0.53, -2.58) * mm});
            skLineSegment(sketch, "E586", {"start": v(-0.53, -2.58) * mm, "end": v(-0.6, -2.6) * mm});
            skLineSegment(sketch, "E587", {"start": v(-0.6, -2.6) * mm, "end": v(-0.62, -2.6) * mm});
            skLineSegment(sketch, "E588", {"start": v(-0.62, -2.6) * mm, "end": v(-0.64, -2.6) * mm});
            skLineSegment(sketch, "E589", {"start": v(-0.64, -2.6) * mm, "end": v(-0.7, -2.58) * mm});
            skLineSegment(sketch, "E590", {"start": v(-0.7, -2.58) * mm, "end": v(-0.7, -2.58) * mm});
            skLineSegment(sketch, "E591", {"start": v(-0.7, -2.58) * mm, "end": v(-0.76, -2.56) * mm});
            skLineSegment(sketch, "E592", {"start": v(-0.76, -2.56) * mm, "end": v(-0.76, -2.56) * mm});
            skLineSegment(sketch, "E593", {"start": v(-0.76, -2.56) * mm, "end": v(-0.77, -2.55) * mm});
            skLineSegment(sketch, "E594", {"start": v(-0.77, -2.55) * mm, "end": v(-0.8, -2.53) * mm});
            skLineSegment(sketch, "E595", {"start": v(-0.8, -2.53) * mm, "end": v(-0.83, -2.5) * mm});
            skLineSegment(sketch, "E596", {"start": v(-0.83, -2.5) * mm, "end": v(-0.83, -2.5) * mm});
            skLineSegment(sketch, "E597", {"start": v(-0.83, -2.5) * mm, "end": v(-0.84, -2.49) * mm});
            skLineSegment(sketch, "E598", {"start": v(-0.3, -1.9) * mm, "end": v(0.2, -1.9) * mm});
            skLineSegment(sketch, "E599", {"start": v(0.2, -1.9) * mm, "end": v(0.22, -1.9) * mm});
            skLineSegment(sketch, "E600", {"start": v(0.22, -1.9) * mm, "end": v(0.25, -1.9) * mm});
            skLineSegment(sketch, "E601", {"start": v(0.25, -1.9) * mm, "end": v(0.25, -1.9) * mm});
            skLineSegment(sketch, "E602", {"start": v(0.25, -1.9) * mm, "end": v(0.26, -1.9) * mm});
            skLineSegment(sketch, "E603", {"start": v(0.26, -1.9) * mm, "end": v(0.27, -1.93) * mm});
            skLineSegment(sketch, "E604", {"start": v(0.27, -1.93) * mm, "end": v(0.27, -1.93) * mm});
            skLineSegment(sketch, "E605", {"start": v(0.27, -1.93) * mm, "end": v(0.28, -1.96) * mm});
            skLineSegment(sketch, "E606", {"start": v(0.28, -1.96) * mm, "end": v(0.28, -1.97) * mm});
            skLineSegment(sketch, "E607", {"start": v(0.28, -1.97) * mm, "end": v(0.28, -1.98) * mm});
            skLineSegment(sketch, "E608", {"start": v(0.28, -1.98) * mm, "end": v(0.27, -2) * mm});
            skLineSegment(sketch, "E609", {"start": v(0.27, -2) * mm, "end": v(0.27, -2) * mm});
            skLineSegment(sketch, "E610", {"start": v(0.27, -2) * mm, "end": v(0.26, -2.02) * mm});
            skLineSegment(sketch, "E611", {"start": v(0.26, -2.02) * mm, "end": v(0.26, -2.03) * mm});
            skLineSegment(sketch, "E612", {"start": v(0.26, -2.03) * mm, "end": v(0.25, -2.03) * mm});
            skLineSegment(sketch, "E613", {"start": v(0.25, -2.03) * mm, "end": v(0.22, -2.03) * mm});
            skLineSegment(sketch, "E614", {"start": v(0.22, -2.03) * mm, "end": v(0.2, -2.03) * mm});
            skLineSegment(sketch, "E615", {"start": v(0.2, -2.03) * mm, "end": v(0.03, -2.03) * mm});
            skLineSegment(sketch, "E616", {"start": v(0.03, -2.03) * mm, "end": v(0.03, -2.5) * mm});
            skLineSegment(sketch, "E617", {"start": v(0.03, -2.5) * mm, "end": v(0.03, -2.51) * mm});
            skLineSegment(sketch, "E618", {"start": v(0.03, -2.51) * mm, "end": v(0.03, -2.53) * mm});
            skLineSegment(sketch, "E619", {"start": v(0.03, -2.53) * mm, "end": v(0.03, -2.54) * mm});
            skLineSegment(sketch, "E620", {"start": v(0.03, -2.54) * mm, "end": v(0.03, -2.54) * mm});
            skLineSegment(sketch, "E621", {"start": v(0.03, -2.54) * mm, "end": v(0.02, -2.56) * mm});
            skLineSegment(sketch, "E622", {"start": v(0.02, -2.56) * mm, "end": v(0.02, -2.56) * mm});
            skLineSegment(sketch, "E623", {"start": v(0.02, -2.56) * mm, "end": v(0, -2.58) * mm});
            skLineSegment(sketch, "E624", {"start": v(0, -2.58) * mm, "end": v(0, -2.58) * mm});
            skLineSegment(sketch, "E625", {"start": v(0, -2.58) * mm, "end": v(-0.04, -2.58) * mm});
            skLineSegment(sketch, "E626", {"start": v(-0.04, -2.58) * mm, "end": v(-0.05, -2.58) * mm});
            skLineSegment(sketch, "E627", {"start": v(-0.05, -2.58) * mm, "end": v(-0.06, -2.58) * mm});
            skLineSegment(sketch, "E628", {"start": v(-0.06, -2.58) * mm, "end": v(-0.1, -2.58) * mm});
            skLineSegment(sketch, "E629", {"start": v(-0.1, -2.58) * mm, "end": v(-0.1, -2.58) * mm});
            skLineSegment(sketch, "E630", {"start": v(-0.1, -2.58) * mm, "end": v(-0.12, -2.56) * mm});
            skLineSegment(sketch, "E631", {"start": v(-0.12, -2.56) * mm, "end": v(-0.12, -2.56) * mm});
            skLineSegment(sketch, "E632", {"start": v(-0.12, -2.56) * mm, "end": v(-0.13, -2.54) * mm});
            skLineSegment(sketch, "E633", {"start": v(-0.13, -2.54) * mm, "end": v(-0.13, -2.54) * mm});
            skLineSegment(sketch, "E634", {"start": v(-0.13, -2.54) * mm, "end": v(-0.13, -2.53) * mm});
            skLineSegment(sketch, "E635", {"start": v(-0.13, -2.53) * mm, "end": v(-0.13, -2.51) * mm});
            skLineSegment(sketch, "E636", {"start": v(-0.13, -2.51) * mm, "end": v(-0.13, -2.5) * mm});
            skLineSegment(sketch, "E637", {"start": v(-0.13, -2.5) * mm, "end": v(-0.13, -2.03) * mm});
            skLineSegment(sketch, "E638", {"start": v(-0.13, -2.03) * mm, "end": v(-0.31, -2.03) * mm});
            skLineSegment(sketch, "E639", {"start": v(-0.31, -2.03) * mm, "end": v(-0.32, -2.03) * mm});
            skLineSegment(sketch, "E640", {"start": v(-0.32, -2.03) * mm, "end": v(-0.35, -2.03) * mm});
            skLineSegment(sketch, "E641", {"start": v(-0.35, -2.03) * mm, "end": v(-0.35, -2.03) * mm});
            skLineSegment(sketch, "E642", {"start": v(-0.35, -2.03) * mm, "end": v(-0.36, -2.03) * mm});
            skLineSegment(sketch, "E643", {"start": v(-0.36, -2.03) * mm, "end": v(-0.37, -2) * mm});
            skLineSegment(sketch, "E644", {"start": v(-0.37, -2) * mm, "end": v(-0.37, -2) * mm});
            skLineSegment(sketch, "E645", {"start": v(-0.37, -2) * mm, "end": v(-0.38, -1.98) * mm});
            skLineSegment(sketch, "E646", {"start": v(-0.38, -1.98) * mm, "end": v(-0.38, -1.97) * mm});
            skLineSegment(sketch, "E647", {"start": v(-0.38, -1.97) * mm, "end": v(-0.38, -1.96) * mm});
            skLineSegment(sketch, "E648", {"start": v(-0.38, -1.96) * mm, "end": v(-0.37, -1.93) * mm});
            skLineSegment(sketch, "E649", {"start": v(-0.37, -1.93) * mm, "end": v(-0.37, -1.93) * mm});
            skLineSegment(sketch, "E650", {"start": v(-0.37, -1.93) * mm, "end": v(-0.37, -1.92) * mm});
            skLineSegment(sketch, "E651", {"start": v(-0.37, -1.92) * mm, "end": v(-0.36, -1.9) * mm});
            skLineSegment(sketch, "E652", {"start": v(-0.36, -1.9) * mm, "end": v(-0.36, -1.9) * mm});
            skLineSegment(sketch, "E653", {"start": v(-0.36, -1.9) * mm, "end": v(-0.35, -1.9) * mm});
            skLineSegment(sketch, "E654", {"start": v(-0.35, -1.9) * mm, "end": v(-0.32, -1.9) * mm});
            skLineSegment(sketch, "E655", {"start": v(-0.32, -1.9) * mm, "end": v(-0.3, -1.9) * mm});
            skLineSegment(sketch, "E656", {"start": v(0.42, -2.24) * mm, "end": v(0.42, -2.26) * mm});
            skLineSegment(sketch, "E657", {"start": v(0.42, -2.26) * mm, "end": v(0.44, -2.32) * mm});
            skLineSegment(sketch, "E658", {"start": v(0.44, -2.32) * mm, "end": v(0.47, -2.37) * mm});
            skLineSegment(sketch, "E659", {"start": v(0.47, -2.37) * mm, "end": v(0.48, -2.38) * mm});
            skLineSegment(sketch, "E660", {"start": v(0.48, -2.38) * mm, "end": v(0.49, -2.39) * mm});
            skLineSegment(sketch, "E661", {"start": v(0.49, -2.39) * mm, "end": v(0.53, -2.42) * mm});
            skLineSegment(sketch, "E662", {"start": v(0.53, -2.42) * mm, "end": v(0.58, -2.43) * mm});
            skLineSegment(sketch, "E663", {"start": v(0.58, -2.43) * mm, "end": v(0.6, -2.43) * mm});
            skLineSegment(sketch, "E664", {"start": v(0.6, -2.43) * mm, "end": v(0.61, -2.43) * mm});
            skLineSegment(sketch, "E665", {"start": v(0.61, -2.43) * mm, "end": v(0.66, -2.42) * mm});
            skLineSegment(sketch, "E666", {"start": v(0.66, -2.42) * mm, "end": v(0.7, -2.39) * mm});
            skLineSegment(sketch, "E667", {"start": v(0.7, -2.39) * mm, "end": v(0.72, -2.38) * mm});
            skLineSegment(sketch, "E668", {"start": v(0.72, -2.38) * mm, "end": v(0.73, -2.37) * mm});
            skLineSegment(sketch, "E669", {"start": v(0.73, -2.37) * mm, "end": v(0.76, -2.32) * mm});
            skLineSegment(sketch, "E670", {"start": v(0.76, -2.32) * mm, "end": v(0.77, -2.26) * mm});
            skLineSegment(sketch, "E671", {"start": v(0.77, -2.26) * mm, "end": v(0.77, -2.24) * mm});
            skLineSegment(sketch, "E672", {"start": v(0.77, -2.24) * mm, "end": v(0.77, -2.23) * mm});
            skLineSegment(sketch, "E673", {"start": v(0.77, -2.23) * mm, "end": v(0.76, -2.17) * mm});
            skLineSegment(sketch, "E674", {"start": v(0.76, -2.17) * mm, "end": v(0.72, -2.12) * mm});
            skLineSegment(sketch, "E675", {"start": v(0.72, -2.12) * mm, "end": v(0.72, -2.1) * mm});
            skLineSegment(sketch, "E676", {"start": v(0.72, -2.1) * mm, "end": v(0.7, -2.1) * mm});
            skLineSegment(sketch, "E677", {"start": v(0.7, -2.1) * mm, "end": v(0.66, -2.07) * mm});
            skLineSegment(sketch, "E678", {"start": v(0.66, -2.07) * mm, "end": v(0.61, -2.06) * mm});
            skLineSegment(sketch, "E679", {"start": v(0.61, -2.06) * mm, "end": v(0.6, -2.06) * mm});
            skLineSegment(sketch, "E680", {"start": v(0.6, -2.06) * mm, "end": v(0.58, -2.06) * mm});
            skLineSegment(sketch, "E681", {"start": v(0.58, -2.06) * mm, "end": v(0.53, -2.07) * mm});
            skLineSegment(sketch, "E682", {"start": v(0.53, -2.07) * mm, "end": v(0.49, -2.1) * mm});
            skLineSegment(sketch, "E683", {"start": v(0.49, -2.1) * mm, "end": v(0.48, -2.1) * mm});
            skLineSegment(sketch, "E684", {"start": v(0.48, -2.1) * mm, "end": v(0.47, -2.12) * mm});
            skLineSegment(sketch, "E685", {"start": v(0.47, -2.12) * mm, "end": v(0.44, -2.17) * mm});
            skLineSegment(sketch, "E686", {"start": v(0.44, -2.17) * mm, "end": v(0.42, -2.22) * mm});
            skLineSegment(sketch, "E687", {"start": v(0.42, -2.22) * mm, "end": v(0.42, -2.24) * mm});
            skLineSegment(sketch, "E688", {"start": v(0.6, -1.9) * mm, "end": v(0.63, -1.9) * mm});
            skLineSegment(sketch, "E689", {"start": v(0.63, -1.9) * mm, "end": v(0.72, -1.92) * mm});
            skLineSegment(sketch, "E690", {"start": v(0.72, -1.92) * mm, "end": v(0.82, -1.97) * mm});
            skLineSegment(sketch, "E691", {"start": v(0.82, -1.97) * mm, "end": v(0.83, -2) * mm});
            skLineSegment(sketch, "E692", {"start": v(0.83, -2) * mm, "end": v(0.85, -2) * mm});
            skLineSegment(sketch, "E693", {"start": v(0.85, -2) * mm, "end": v(0.9, -2.1) * mm});
            skLineSegment(sketch, "E694", {"start": v(0.9, -2.1) * mm, "end": v(0.93, -2.2) * mm});
            skLineSegment(sketch, "E695", {"start": v(0.93, -2.2) * mm, "end": v(0.93, -2.24) * mm});
            skLineSegment(sketch, "E696", {"start": v(0.93, -2.24) * mm, "end": v(0.93, -2.27) * mm});
            skLineSegment(sketch, "E697", {"start": v(0.93, -2.27) * mm, "end": v(0.91, -2.38) * mm});
            skLineSegment(sketch, "E698", {"start": v(0.91, -2.38) * mm, "end": v(0.85, -2.47) * mm});
            skLineSegment(sketch, "E699", {"start": v(0.85, -2.47) * mm, "end": v(0.84, -2.5) * mm});
            skLineSegment(sketch, "E700", {"start": v(0.84, -2.5) * mm, "end": v(0.82, -2.5) * mm});
            skLineSegment(sketch, "E701", {"start": v(0.82, -2.5) * mm, "end": v(0.73, -2.57) * mm});
            skLineSegment(sketch, "E702", {"start": v(0.73, -2.57) * mm, "end": v(0.63, -2.6) * mm});
            skLineSegment(sketch, "E703", {"start": v(0.63, -2.6) * mm, "end": v(0.6, -2.6) * mm});
            skLineSegment(sketch, "E704", {"start": v(0.6, -2.6) * mm, "end": v(0.57, -2.6) * mm});
            skLineSegment(sketch, "E705", {"start": v(0.57, -2.6) * mm, "end": v(0.47, -2.57) * mm});
            skLineSegment(sketch, "E706", {"start": v(0.47, -2.57) * mm, "end": v(0.37, -2.5) * mm});
            skLineSegment(sketch, "E707", {"start": v(0.37, -2.5) * mm, "end": v(0.36, -2.5) * mm});
            skLineSegment(sketch, "E708", {"start": v(0.36, -2.5) * mm, "end": v(0.34, -2.48) * mm});
            skLineSegment(sketch, "E709", {"start": v(0.34, -2.48) * mm, "end": v(0.28, -2.38) * mm});
            skLineSegment(sketch, "E710", {"start": v(0.28, -2.38) * mm, "end": v(0.26, -2.28) * mm});
            skLineSegment(sketch, "E711", {"start": v(0.26, -2.28) * mm, "end": v(0.26, -2.25) * mm});
            skLineSegment(sketch, "E712", {"start": v(0.26, -2.25) * mm, "end": v(0.26, -2.23) * mm});
            skLineSegment(sketch, "E713", {"start": v(0.26, -2.23) * mm, "end": v(0.27, -2.17) * mm});
            skLineSegment(sketch, "E714", {"start": v(0.27, -2.17) * mm, "end": v(0.28, -2.11) * mm});
            skLineSegment(sketch, "E715", {"start": v(0.28, -2.11) * mm, "end": v(0.29, -2.1) * mm});
            skLineSegment(sketch, "E716", {"start": v(0.29, -2.1) * mm, "end": v(0.3, -2.1) * mm});
            skLineSegment(sketch, "E717", {"start": v(0.3, -2.1) * mm, "end": v(0.32, -2.04) * mm});
            skLineSegment(sketch, "E718", {"start": v(0.32, -2.04) * mm, "end": v(0.35, -2) * mm});
            skLineSegment(sketch, "E719", {"start": v(0.35, -2) * mm, "end": v(0.36, -1.99) * mm});
            skLineSegment(sketch, "E720", {"start": v(0.36, -1.99) * mm, "end": v(0.37, -1.98) * mm});
            skLineSegment(sketch, "E721", {"start": v(0.37, -1.98) * mm, "end": v(0.41, -1.95) * mm});
            skLineSegment(sketch, "E722", {"start": v(0.41, -1.95) * mm, "end": v(0.46, -1.92) * mm});
            skLineSegment(sketch, "E723", {"start": v(0.46, -1.92) * mm, "end": v(0.47, -1.92) * mm});
            skLineSegment(sketch, "E724", {"start": v(0.47, -1.92) * mm, "end": v(0.48, -1.91) * mm});
            skLineSegment(sketch, "E725", {"start": v(0.48, -1.91) * mm, "end": v(0.53, -1.9) * mm});
            skLineSegment(sketch, "E726", {"start": v(0.53, -1.9) * mm, "end": v(0.58, -1.9) * mm});
            skLineSegment(sketch, "E727", {"start": v(0.58, -1.9) * mm, "end": v(0.6, -1.9) * mm});
            skLineSegment(sketch, "E728", {"start": v(1.14, -2.43) * mm, "end": v(1.14, -2.43) * mm});
            skLineSegment(sketch, "E729", {"start": v(1.14, -2.43) * mm, "end": v(1.15, -2.45) * mm});
            skLineSegment(sketch, "E730", {"start": v(1.15, -2.45) * mm, "end": v(1.16, -2.49) * mm});
            skLineSegment(sketch, "E731", {"start": v(1.16, -2.49) * mm, "end": v(1.16, -2.5) * mm});
            skLineSegment(sketch, "E732", {"start": v(1.16, -2.5) * mm, "end": v(1.16, -2.5) * mm});
            skLineSegment(sketch, "E733", {"start": v(1.16, -2.5) * mm, "end": v(1.15, -2.53) * mm});
            skLineSegment(sketch, "E734", {"start": v(1.15, -2.53) * mm, "end": v(1.15, -2.53) * mm});
            skLineSegment(sketch, "E735", {"start": v(1.15, -2.53) * mm, "end": v(1.15, -2.56) * mm});
            skLineSegment(sketch, "E736", {"start": v(1.15, -2.56) * mm, "end": v(1.14, -2.56) * mm});
            skLineSegment(sketch, "E737", {"start": v(1.14, -2.56) * mm, "end": v(1.14, -2.56) * mm});
            skLineSegment(sketch, "E738", {"start": v(1.14, -2.56) * mm, "end": v(1.12, -2.58) * mm});
            skLineSegment(sketch, "E739", {"start": v(1.12, -2.58) * mm, "end": v(1.09, -2.59) * mm});
            skLineSegment(sketch, "E740", {"start": v(1.09, -2.59) * mm, "end": v(1.07, -2.59) * mm});
            skLineSegment(sketch, "E741", {"start": v(1.07, -2.59) * mm, "end": v(1.06, -2.59) * mm});
            skLineSegment(sketch, "E742", {"start": v(1.06, -2.59) * mm, "end": v(1.03, -2.58) * mm});
            skLineSegment(sketch, "E743", {"start": v(1.03, -2.58) * mm, "end": v(1, -2.57) * mm});
            skLineSegment(sketch, "E744", {"start": v(1, -2.57) * mm, "end": v(1, -2.57) * mm});
            skLineSegment(sketch, "E745", {"start": v(1, -2.57) * mm, "end": v(1, -2.56) * mm});
            skLineSegment(sketch, "E746", {"start": v(1, -2.56) * mm, "end": v(0.99, -2.54) * mm});
            skLineSegment(sketch, "E747", {"start": v(0.99, -2.54) * mm, "end": v(0.98, -2.51) * mm});
            skLineSegment(sketch, "E748", {"start": v(0.98, -2.51) * mm, "end": v(0.98, -2.5) * mm});
            skLineSegment(sketch, "E749", {"start": v(0.98, -2.5) * mm, "end": v(0.98, -2.5) * mm});
            skLineSegment(sketch, "E750", {"start": v(0.98, -2.5) * mm, "end": v(0.98, -2.49) * mm});
            skLineSegment(sketch, "E751", {"start": v(0.98, -2.49) * mm, "end": v(0.98, -2.47) * mm});
            skLineSegment(sketch, "E752", {"start": v(0.98, -2.47) * mm, "end": v(0.98, -2.46) * mm});
            skLineSegment(sketch, "E753", {"start": v(0.98, -2.46) * mm, "end": v(0.98, -2.46) * mm});
            skLineSegment(sketch, "E754", {"start": v(0.98, -2.46) * mm, "end": v(1, -2.44) * mm});
            skLineSegment(sketch, "E755", {"start": v(1, -2.44) * mm, "end": v(1, -2.44) * mm});
            skLineSegment(sketch, "E756", {"start": v(1, -2.44) * mm, "end": v(1, -2.43) * mm});
            skLineSegment(sketch, "E757", {"start": v(1, -2.43) * mm, "end": v(1.02, -2.42) * mm});
            skLineSegment(sketch, "E758", {"start": v(1.02, -2.42) * mm, "end": v(1.05, -2.41) * mm});
            skLineSegment(sketch, "E759", {"start": v(1.05, -2.41) * mm, "end": v(1.06, -2.41) * mm});
            skLineSegment(sketch, "E760", {"start": v(1.06, -2.41) * mm, "end": v(1.07, -2.41) * mm});
            skLineSegment(sketch, "E761", {"start": v(1.07, -2.41) * mm, "end": v(1.1, -2.42) * mm});
            skLineSegment(sketch, "E762", {"start": v(1.1, -2.42) * mm, "end": v(1.14, -2.43) * mm});
            skLineSegment(sketch, "E763", {"start": v(1.22, -1.98) * mm, "end": v(1.22, -1.97) * mm});
            skLineSegment(sketch, "E764", {"start": v(1.22, -1.97) * mm, "end": v(1.22, -1.95) * mm});
            skLineSegment(sketch, "E765", {"start": v(1.22, -1.95) * mm, "end": v(1.22, -1.95) * mm});
            skLineSegment(sketch, "E766", {"start": v(1.22, -1.95) * mm, "end": v(1.23, -1.93) * mm});
            skLineSegment(sketch, "E767", {"start": v(1.23, -1.93) * mm, "end": v(1.23, -1.93) * mm});
            skLineSegment(sketch, "E768", {"start": v(1.23, -1.93) * mm, "end": v(1.23, -1.92) * mm});
            skLineSegment(sketch, "E769", {"start": v(1.23, -1.92) * mm, "end": v(1.25, -1.9) * mm});
            skLineSegment(sketch, "E770", {"start": v(1.25, -1.9) * mm, "end": v(1.29, -1.9) * mm});
            skLineSegment(sketch, "E771", {"start": v(1.29, -1.9) * mm, "end": v(1.3, -1.9) * mm});
            skLineSegment(sketch, "E772", {"start": v(1.3, -1.9) * mm, "end": v(1.31, -1.9) * mm});
            skLineSegment(sketch, "E773", {"start": v(1.31, -1.9) * mm, "end": v(1.35, -1.9) * mm});
            skLineSegment(sketch, "E774", {"start": v(1.35, -1.9) * mm, "end": v(1.38, -1.93) * mm});
            skLineSegment(sketch, "E775", {"start": v(1.38, -1.93) * mm, "end": v(1.38, -1.93) * mm});
            skLineSegment(sketch, "E776", {"start": v(1.38, -1.93) * mm, "end": v(1.38, -1.94) * mm});
            skLineSegment(sketch, "E777", {"start": v(1.38, -1.94) * mm, "end": v(1.38, -1.97) * mm});
            skLineSegment(sketch, "E778", {"start": v(1.38, -1.97) * mm, "end": v(1.38, -1.98) * mm});
            skLineSegment(sketch, "E779", {"start": v(1.38, -1.98) * mm, "end": v(1.38, -2.5) * mm});
            skLineSegment(sketch, "E780", {"start": v(1.38, -2.5) * mm, "end": v(1.38, -2.51) * mm});
            skLineSegment(sketch, "E781", {"start": v(1.38, -2.51) * mm, "end": v(1.38, -2.53) * mm});
            skLineSegment(sketch, "E782", {"start": v(1.38, -2.53) * mm, "end": v(1.38, -2.53) * mm});
            skLineSegment(sketch, "E783", {"start": v(1.38, -2.53) * mm, "end": v(1.38, -2.54) * mm});
            skLineSegment(sketch, "E784", {"start": v(1.38, -2.54) * mm, "end": v(1.37, -2.56) * mm});
            skLineSegment(sketch, "E785", {"start": v(1.37, -2.56) * mm, "end": v(1.37, -2.56) * mm});
            skLineSegment(sketch, "E786", {"start": v(1.37, -2.56) * mm, "end": v(1.35, -2.58) * mm});
            skLineSegment(sketch, "E787", {"start": v(1.35, -2.58) * mm, "end": v(1.31, -2.58) * mm});
            skLineSegment(sketch, "E788", {"start": v(1.31, -2.58) * mm, "end": v(1.3, -2.58) * mm});
            skLineSegment(sketch, "E789", {"start": v(1.3, -2.58) * mm, "end": v(1.29, -2.58) * mm});
            skLineSegment(sketch, "E790", {"start": v(1.29, -2.58) * mm, "end": v(1.25, -2.58) * mm});
            skLineSegment(sketch, "E791", {"start": v(1.25, -2.58) * mm, "end": v(1.22, -2.55) * mm});
            skLineSegment(sketch, "E792", {"start": v(1.22, -2.55) * mm, "end": v(1.22, -2.55) * mm});
            skLineSegment(sketch, "E793", {"start": v(1.22, -2.55) * mm, "end": v(1.22, -2.51) * mm});
            skLineSegment(sketch, "E794", {"start": v(1.22, -2.51) * mm, "end": v(1.22, -2.5) * mm});
            skLineSegment(sketch, "E795", {"start": v(1.22, -2.5) * mm, "end": v(1.22, -1.98) * mm});
            skLineSegment(sketch, "E796", {"start": v(1.6, -2.24) * mm, "end": v(1.6, -2.26) * mm});
            skLineSegment(sketch, "E797", {"start": v(1.6, -2.26) * mm, "end": v(1.62, -2.32) * mm});
            skLineSegment(sketch, "E798", {"start": v(1.62, -2.32) * mm, "end": v(1.65, -2.37) * mm});
            skLineSegment(sketch, "E799", {"start": v(1.65, -2.37) * mm, "end": v(1.66, -2.38) * mm});
            skLineSegment(sketch, "E800", {"start": v(1.66, -2.38) * mm, "end": v(1.67, -2.39) * mm});
            skLineSegment(sketch, "E801", {"start": v(1.67, -2.39) * mm, "end": v(1.72, -2.42) * mm});
            skLineSegment(sketch, "E802", {"start": v(1.72, -2.42) * mm, "end": v(1.77, -2.43) * mm});
            skLineSegment(sketch, "E803", {"start": v(1.77, -2.43) * mm, "end": v(1.78, -2.43) * mm});
            skLineSegment(sketch, "E804", {"start": v(1.78, -2.43) * mm, "end": v(1.8, -2.43) * mm});
            skLineSegment(sketch, "E805", {"start": v(1.8, -2.43) * mm, "end": v(1.84, -2.42) * mm});
            skLineSegment(sketch, "E806", {"start": v(1.84, -2.42) * mm, "end": v(1.9, -2.39) * mm});
            skLineSegment(sketch, "E807", {"start": v(1.9, -2.39) * mm, "end": v(1.9, -2.38) * mm});
            skLineSegment(sketch, "E808", {"start": v(1.9, -2.38) * mm, "end": v(1.9, -2.37) * mm});
            skLineSegment(sketch, "E809", {"start": v(1.9, -2.37) * mm, "end": v(1.94, -2.32) * mm});
            skLineSegment(sketch, "E810", {"start": v(1.94, -2.32) * mm, "end": v(1.95, -2.26) * mm});
            skLineSegment(sketch, "E811", {"start": v(1.95, -2.26) * mm, "end": v(1.95, -2.24) * mm});
            skLineSegment(sketch, "E812", {"start": v(1.95, -2.24) * mm, "end": v(1.95, -2.23) * mm});
            skLineSegment(sketch, "E813", {"start": v(1.95, -2.23) * mm, "end": v(1.94, -2.17) * mm});
            skLineSegment(sketch, "E814", {"start": v(1.94, -2.17) * mm, "end": v(1.9, -2.12) * mm});
            skLineSegment(sketch, "E815", {"start": v(1.9, -2.12) * mm, "end": v(1.9, -2.1) * mm});
            skLineSegment(sketch, "E816", {"start": v(1.9, -2.1) * mm, "end": v(1.9, -2.1) * mm});
            skLineSegment(sketch, "E817", {"start": v(1.9, -2.1) * mm, "end": v(1.84, -2.07) * mm});
            skLineSegment(sketch, "E818", {"start": v(1.84, -2.07) * mm, "end": v(1.8, -2.06) * mm});
            skLineSegment(sketch, "E819", {"start": v(1.8, -2.06) * mm, "end": v(1.78, -2.06) * mm});
            skLineSegment(sketch, "E820", {"start": v(1.78, -2.06) * mm, "end": v(1.76, -2.06) * mm});
            skLineSegment(sketch, "E821", {"start": v(1.76, -2.06) * mm, "end": v(1.72, -2.07) * mm});
            skLineSegment(sketch, "E822", {"start": v(1.72, -2.07) * mm, "end": v(1.67, -2.1) * mm});
            skLineSegment(sketch, "E823", {"start": v(1.67, -2.1) * mm, "end": v(1.66, -2.1) * mm});
            skLineSegment(sketch, "E824", {"start": v(1.66, -2.1) * mm, "end": v(1.65, -2.12) * mm});
            skLineSegment(sketch, "E825", {"start": v(1.65, -2.12) * mm, "end": v(1.62, -2.17) * mm});
            skLineSegment(sketch, "E826", {"start": v(1.62, -2.17) * mm, "end": v(1.6, -2.22) * mm});
            skLineSegment(sketch, "E827", {"start": v(1.6, -2.22) * mm, "end": v(1.6, -2.24) * mm});
            skLineSegment(sketch, "E828", {"start": v(1.78, -1.9) * mm, "end": v(1.8, -1.9) * mm});
            skLineSegment(sketch, "E829", {"start": v(1.8, -1.9) * mm, "end": v(1.9, -1.92) * mm});
            skLineSegment(sketch, "E830", {"start": v(1.9, -1.92) * mm, "end": v(2, -1.97) * mm});
            skLineSegment(sketch, "E831", {"start": v(2, -1.97) * mm, "end": v(2.02, -2) * mm});
            skLineSegment(sketch, "E832", {"start": v(2.02, -2) * mm, "end": v(2.03, -2) * mm});
            skLineSegment(sketch, "E833", {"start": v(2.03, -2) * mm, "end": v(2.1, -2.1) * mm});
            skLineSegment(sketch, "E834", {"start": v(2.1, -2.1) * mm, "end": v(2.12, -2.2) * mm});
            skLineSegment(sketch, "E835", {"start": v(2.12, -2.2) * mm, "end": v(2.12, -2.24) * mm});
            skLineSegment(sketch, "E836", {"start": v(2.12, -2.24) * mm, "end": v(2.12, -2.27) * mm});
            skLineSegment(sketch, "E837", {"start": v(2.12, -2.27) * mm, "end": v(2.1, -2.38) * mm});
            skLineSegment(sketch, "E838", {"start": v(2.1, -2.38) * mm, "end": v(2.04, -2.47) * mm});
            skLineSegment(sketch, "E839", {"start": v(2.04, -2.47) * mm, "end": v(2.02, -2.5) * mm});
            skLineSegment(sketch, "E840", {"start": v(2.02, -2.5) * mm, "end": v(2, -2.5) * mm});
            skLineSegment(sketch, "E841", {"start": v(2, -2.5) * mm, "end": v(1.91, -2.57) * mm});
            skLineSegment(sketch, "E842", {"start": v(1.91, -2.57) * mm, "end": v(1.82, -2.6) * mm});
            skLineSegment(sketch, "E843", {"start": v(1.82, -2.6) * mm, "end": v(1.78, -2.6) * mm});
            skLineSegment(sketch, "E844", {"start": v(1.78, -2.6) * mm, "end": v(1.75, -2.6) * mm});
            skLineSegment(sketch, "E845", {"start": v(1.75, -2.6) * mm, "end": v(1.65, -2.57) * mm});
            skLineSegment(sketch, "E846", {"start": v(1.65, -2.57) * mm, "end": v(1.56, -2.5) * mm});
            skLineSegment(sketch, "E847", {"start": v(1.56, -2.5) * mm, "end": v(1.54, -2.5) * mm});
            skLineSegment(sketch, "E848", {"start": v(1.54, -2.5) * mm, "end": v(1.53, -2.48) * mm});
            skLineSegment(sketch, "E849", {"start": v(1.53, -2.48) * mm, "end": v(1.47, -2.38) * mm});
            skLineSegment(sketch, "E850", {"start": v(1.47, -2.38) * mm, "end": v(1.44, -2.28) * mm});
            skLineSegment(sketch, "E851", {"start": v(1.44, -2.28) * mm, "end": v(1.44, -2.25) * mm});
            skLineSegment(sketch, "E852", {"start": v(1.44, -2.25) * mm, "end": v(1.44, -2.23) * mm});
            skLineSegment(sketch, "E853", {"start": v(1.44, -2.23) * mm, "end": v(1.45, -2.17) * mm});
            skLineSegment(sketch, "E854", {"start": v(1.45, -2.17) * mm, "end": v(1.47, -2.11) * mm});
            skLineSegment(sketch, "E855", {"start": v(1.47, -2.11) * mm, "end": v(1.47, -2.1) * mm});
            skLineSegment(sketch, "E856", {"start": v(1.47, -2.1) * mm, "end": v(1.48, -2.1) * mm});
            skLineSegment(sketch, "E857", {"start": v(1.48, -2.1) * mm, "end": v(1.5, -2.04) * mm});
            skLineSegment(sketch, "E858", {"start": v(1.5, -2.04) * mm, "end": v(1.54, -2) * mm});
            skLineSegment(sketch, "E859", {"start": v(1.54, -2) * mm, "end": v(1.55, -1.99) * mm});
            skLineSegment(sketch, "E860", {"start": v(1.55, -1.99) * mm, "end": v(1.55, -1.98) * mm});
            skLineSegment(sketch, "E861", {"start": v(1.55, -1.98) * mm, "end": v(1.6, -1.95) * mm});
            skLineSegment(sketch, "E862", {"start": v(1.6, -1.95) * mm, "end": v(1.64, -1.92) * mm});
            skLineSegment(sketch, "E863", {"start": v(1.64, -1.92) * mm, "end": v(1.65, -1.92) * mm});
            skLineSegment(sketch, "E864", {"start": v(1.65, -1.92) * mm, "end": v(1.66, -1.91) * mm});
            skLineSegment(sketch, "E865", {"start": v(1.66, -1.91) * mm, "end": v(1.71, -1.9) * mm});
            skLineSegment(sketch, "E866", {"start": v(1.71, -1.9) * mm, "end": v(1.76, -1.9) * mm});
            skLineSegment(sketch, "E867", {"start": v(1.76, -1.9) * mm, "end": v(1.78, -1.9) * mm});
            skLineSegment(sketch, "E868.bottom", {"start": v(10, -10) * mm, "end": v(-10, -10) * mm});
            skLineSegment(sketch, "E868.top", {"start": v(10, 10) * mm, "end": v(-10, 10) * mm});
            skLineSegment(sketch, "E868.left", {"start": v(10, -10) * mm, "end": v(10, 10) * mm});
            skLineSegment(sketch, "E868.right", {"start": v(-10, -10) * mm, "end": v(-10, 10) * mm});
            skPoint(sketch, "E868.middle", {"position": v(0, 0) * mm});
            skSolve(sketch);
        }
        {
            var Q0;
            Q0=makeQuery(id+"F0.imprint","IMPRINT",FACE,{"disambiguationData":[TD([[makeQuery(id+"F0.imprint","IMPRINT",EDGE,{"derivedFrom":sQuery(id+"F0.wireOp",EDGE,"E222")}),-1.0]])]});
            var Q1;
            Q1=makeQuery(id+"F0.imprint","IMPRINT",FACE,{"disambiguationData":[TD([[makeQuery(id+"F0.imprint","IMPRINT",EDGE,{"derivedFrom":sQuery(id+"F0.wireOp",EDGE,"E37")}),-1.0]])]});
            var Q2;
            Q2=makeQuery(id+"F0.imprint","IMPRINT",FACE,{"disambiguationData":[TD([[makeQuery(id+"F0.imprint","IMPRINT",EDGE,{"derivedFrom":sQuery(id+"F0.wireOp",EDGE,"E102")}),-1.0]])]});
            var Q3;
            Q3=makeQuery(id+"F0.imprint","IMPRINT",FACE,{"disambiguationData":[TD([[makeQuery(id+"F0.imprint","IMPRINT",EDGE,{"derivedFrom":sQuery(id+"F0.wireOp",EDGE,"E0")}),-1.0]])]});
            extrude(context, id + "F1", {"entities" : qUnion([Q0, Q1, Q2, Q3]), "depth" : (0.6 / 4) * mm, "offsetDistance" : 25 * mm});
        }
        {
            var Q0;
            Q0=makeQuery(id+"F1.opExtrude","SWEPT_BODY",BODY,{"disambiguationData":[OSD([sQuery(id+"F0.wireOp",EDGE,"E222"),sQuery(id+"F0.wireOp",EDGE,"E223"),sQuery(id+"F0.wireOp",EDGE,"E224"),sQuery(id+"F0.wireOp",EDGE,"E225"),sQuery(id+"F0.wireOp",EDGE,"E226"),sQuery(id+"F0.wireOp",EDGE,"E227"),sQuery(id+"F0.wireOp",EDGE,"E228"),sQuery(id+"F0.wireOp",EDGE,"E229"),sQuery(id+"F0.wireOp",EDGE,"E230"),sQuery(id+"F0.wireOp",EDGE,"E231"),sQuery(id+"F0.wireOp",EDGE,"E232"),sQuery(id+"F0.wireOp",EDGE,"E233"),sQuery(id+"F0.wireOp",EDGE,"E234"),sQuery(id+"F0.wireOp",EDGE,"E235"),sQuery(id+"F0.wireOp",EDGE,"E236"),sQuery(id+"F0.wireOp",EDGE,"E237"),sQuery(id+"F0.wireOp",EDGE,"E238"),sQuery(id+"F0.wireOp",EDGE,"E239"),sQuery(id+"F0.wireOp",EDGE,"E240"),sQuery(id+"F0.wireOp",EDGE,"E241"),sQuery(id+"F0.wireOp",EDGE,"E242"),sQuery(id+"F0.wireOp",EDGE,"E243"),sQuery(id+"F0.wireOp",EDGE,"E244"),sQuery(id+"F0.wireOp",EDGE,"E245"),sQuery(id+"F0.wireOp",EDGE,"E246"),sQuery(id+"F0.wireOp",EDGE,"E247"),sQuery(id+"F0.wireOp",EDGE,"E248"),sQuery(id+"F0.wireOp",EDGE,"E249"),sQuery(id+"F0.wireOp",EDGE,"E250"),sQuery(id+"F0.wireOp",EDGE,"E251"),sQuery(id+"F0.wireOp",EDGE,"E252"),sQuery(id+"F0.wireOp",EDGE,"E253"),sQuery(id+"F0.wireOp",EDGE,"E254"),sQuery(id+"F0.wireOp",EDGE,"E255"),sQuery(id+"F0.wireOp",EDGE,"E256"),sQuery(id+"F0.wireOp",EDGE,"E257"),sQuery(id+"F0.wireOp",EDGE,"E258"),sQuery(id+"F0.wireOp",EDGE,"E259"),sQuery(id+"F0.wireOp",EDGE,"E260"),sQuery(id+"F0.wireOp",EDGE,"E261")])]});
            var Q1;
            Q1=makeQuery(id+"F1.opExtrude","SWEPT_BODY",BODY,{"disambiguationData":[OSD([sQuery(id+"F0.wireOp",EDGE,"E37"),sQuery(id+"F0.wireOp",EDGE,"E38"),sQuery(id+"F0.wireOp",EDGE,"E39"),sQuery(id+"F0.wireOp",EDGE,"E40"),sQuery(id+"F0.wireOp",EDGE,"E41"),sQuery(id+"F0.wireOp",EDGE,"E42"),sQuery(id+"F0.wireOp",EDGE,"E43"),sQuery(id+"F0.wireOp",EDGE,"E44"),sQuery(id+"F0.wireOp",EDGE,"E45"),sQuery(id+"F0.wireOp",EDGE,"E46"),sQuery(id+"F0.wireOp",EDGE,"E47"),sQuery(id+"F0.wireOp",EDGE,"E48"),sQuery(id+"F0.wireOp",EDGE,"E49"),sQuery(id+"F0.wireOp",EDGE,"E50"),sQuery(id+"F0.wireOp",EDGE,"E51"),sQuery(id+"F0.wireOp",EDGE,"E52"),sQuery(id+"F0.wireOp",EDGE,"E53"),sQuery(id+"F0.wireOp",EDGE,"E54"),sQuery(id+"F0.wireOp",EDGE,"E55"),sQuery(id+"F0.wireOp",EDGE,"E56"),sQuery(id+"F0.wireOp",EDGE,"E57"),sQuery(id+"F0.wireOp",EDGE,"E58"),sQuery(id+"F0.wireOp",EDGE,"E59"),sQuery(id+"F0.wireOp",EDGE,"E60"),sQuery(id+"F0.wireOp",EDGE,"E61"),sQuery(id+"F0.wireOp",EDGE,"E62"),sQuery(id+"F0.wireOp",EDGE,"E63"),sQuery(id+"F0.wireOp",EDGE,"E64"),sQuery(id+"F0.wireOp",EDGE,"E65"),sQuery(id+"F0.wireOp",EDGE,"E66"),sQuery(id+"F0.wireOp",EDGE,"E67"),sQuery(id+"F0.wireOp",EDGE,"E68"),sQuery(id+"F0.wireOp",EDGE,"E69"),sQuery(id+"F0.wireOp",EDGE,"E70"),sQuery(id+"F0.wireOp",EDGE,"E71"),sQuery(id+"F0.wireOp",EDGE,"E72"),sQuery(id+"F0.wireOp",EDGE,"E73"),sQuery(id+"F0.wireOp",EDGE,"E74"),sQuery(id+"F0.wireOp",EDGE,"E75"),sQuery(id+"F0.wireOp",EDGE,"E76"),sQuery(id+"F0.wireOp",EDGE,"E77"),sQuery(id+"F0.wireOp",EDGE,"E78"),sQuery(id+"F0.wireOp",EDGE,"E81"),sQuery(id+"F0.wireOp",EDGE,"E82"),sQuery(id+"F0.wireOp",EDGE,"E83"),sQuery(id+"F0.wireOp",EDGE,"E84"),sQuery(id+"F0.wireOp",EDGE,"E85"),sQuery(id+"F0.wireOp",EDGE,"E86"),sQuery(id+"F0.wireOp",EDGE,"E87"),sQuery(id+"F0.wireOp",EDGE,"E88"),sQuery(id+"F0.wireOp",EDGE,"E89"),sQuery(id+"F0.wireOp",EDGE,"E90"),sQuery(id+"F0.wireOp",EDGE,"E91"),sQuery(id+"F0.wireOp",EDGE,"E92"),sQuery(id+"F0.wireOp",EDGE,"E93"),sQuery(id+"F0.wireOp",EDGE,"E94"),sQuery(id+"F0.wireOp",EDGE,"E95"),sQuery(id+"F0.wireOp",EDGE,"E96"),sQuery(id+"F0.wireOp",EDGE,"E97"),sQuery(id+"F0.wireOp",EDGE,"E98"),sQuery(id+"F0.wireOp",EDGE,"E99"),sQuery(id+"F0.wireOp",EDGE,"E100"),sQuery(id+"F0.wireOp",EDGE,"E101")])]});
            var Q2;
            Q2=makeQuery(id+"F1.opExtrude","SWEPT_BODY",BODY,{"disambiguationData":[OSD([sQuery(id+"F0.wireOp",EDGE,"E102"),sQuery(id+"F0.wireOp",EDGE,"E103"),sQuery(id+"F0.wireOp",EDGE,"E104"),sQuery(id+"F0.wireOp",EDGE,"E105"),sQuery(id+"F0.wireOp",EDGE,"E106"),sQuery(id+"F0.wireOp",EDGE,"E107"),sQuery(id+"F0.wireOp",EDGE,"E108"),sQuery(id+"F0.wireOp",EDGE,"E109"),sQuery(id+"F0.wireOp",EDGE,"E110"),sQuery(id+"F0.wireOp",EDGE,"E111"),sQuery(id+"F0.wireOp",EDGE,"E112"),sQuery(id+"F0.wireOp",EDGE,"E113"),sQuery(id+"F0.wireOp",EDGE,"E114"),sQuery(id+"F0.wireOp",EDGE,"E115"),sQuery(id+"F0.wireOp",EDGE,"E116"),sQuery(id+"F0.wireOp",EDGE,"E117"),sQuery(id+"F0.wireOp",EDGE,"E118"),sQuery(id+"F0.wireOp",EDGE,"E119"),sQuery(id+"F0.wireOp",EDGE,"E120"),sQuery(id+"F0.wireOp",EDGE,"E121"),sQuery(id+"F0.wireOp",EDGE,"E122"),sQuery(id+"F0.wireOp",EDGE,"E123"),sQuery(id+"F0.wireOp",EDGE,"E124"),sQuery(id+"F0.wireOp",EDGE,"E125"),sQuery(id+"F0.wireOp",EDGE,"E126"),sQuery(id+"F0.wireOp",EDGE,"E127"),sQuery(id+"F0.wireOp",EDGE,"E128")])]});
            var Q3;
            Q3=makeQuery(id+"F1.opExtrude","SWEPT_BODY",BODY,{"disambiguationData":[OSD([sQuery(id+"F0.wireOp",EDGE,"E0"),sQuery(id+"F0.wireOp",EDGE,"E1"),sQuery(id+"F0.wireOp",EDGE,"E2"),sQuery(id+"F0.wireOp",EDGE,"E3"),sQuery(id+"F0.wireOp",EDGE,"E4"),sQuery(id+"F0.wireOp",EDGE,"E5"),sQuery(id+"F0.wireOp",EDGE,"E6"),sQuery(id+"F0.wireOp",EDGE,"E7"),sQuery(id+"F0.wireOp",EDGE,"E8"),sQuery(id+"F0.wireOp",EDGE,"E9"),sQuery(id+"F0.wireOp",EDGE,"E10"),sQuery(id+"F0.wireOp",EDGE,"E11"),sQuery(id+"F0.wireOp",EDGE,"E12"),sQuery(id+"F0.wireOp",EDGE,"E13"),sQuery(id+"F0.wireOp",EDGE,"E14"),sQuery(id+"F0.wireOp",EDGE,"E15"),sQuery(id+"F0.wireOp",EDGE,"E16"),sQuery(id+"F0.wireOp",EDGE,"E17"),sQuery(id+"F0.wireOp",EDGE,"E18"),sQuery(id+"F0.wireOp",EDGE,"E19"),sQuery(id+"F0.wireOp",EDGE,"E20"),sQuery(id+"F0.wireOp",EDGE,"E21"),sQuery(id+"F0.wireOp",EDGE,"E22"),sQuery(id+"F0.wireOp",EDGE,"E23"),sQuery(id+"F0.wireOp",EDGE,"E24"),sQuery(id+"F0.wireOp",EDGE,"E25"),sQuery(id+"F0.wireOp",EDGE,"E26"),sQuery(id+"F0.wireOp",EDGE,"E27"),sQuery(id+"F0.wireOp",EDGE,"E28"),sQuery(id+"F0.wireOp",EDGE,"E29"),sQuery(id+"F0.wireOp",EDGE,"E30"),sQuery(id+"F0.wireOp",EDGE,"E31"),sQuery(id+"F0.wireOp",EDGE,"E32"),sQuery(id+"F0.wireOp",EDGE,"E33"),sQuery(id+"F0.wireOp",EDGE,"E34"),sQuery(id+"F0.wireOp",EDGE,"E35"),sQuery(id+"F0.wireOp",EDGE,"E36")])]});
            var Q4;
            Q4=qCreatedBy(makeId("Origin.pointOp"),VERTEX);
            transform(context, id + "F2", {"entities" : qUnion([Q0, Q1, Q2, Q3]), "transformType" : TransformType.SCALE_UNIFORMLY, "scale" : 4, "scalePoint" : qUnion([Q4]), "makeCopy" : false});
        }
    });
